FREECAD ASSEMBLY — COMPONENT RECIPES ("composit_stand9")

This assembly document has 29 components, labeled P0..P28 below (a component is one placed body or linked part). 28 of them carry a construction recipe — the FreeCAD feature program that regenerates the part from scratch, quoted from this document or its linked companion documents; the rest are supplied as boundary geometry only. No exploded tour is included for this assembly.
COMPONENT P0 — recipe-attached ("back", modeled in this document).
Construction recipe (the document's own serialized feature program — sketch geometry with constraints, then the solid features built on it; lengths are millimeters unless a unit is written):

FEATURE [PartDesign::SubShapeBinder] Binder001
  BindCopyOnChange = 0
  BindMode = 0
  ClaimChildren = true
  Context = -> Body001 [Binder001.]
  Fuse = false
  MakeFace = true
  OffsetFill = false
  OffsetIntersection = false
  OffsetJoinType = 0
  OffsetOpenResult = false
  PartialLoad = false
  Relative = false
  Support = -> [Connect001]
  _Version = 2
FEATURE [PartDesign::FeaturePython] BaseBend001  # WARN: FeaturePython — macro-defined, semantics opaque (R4)
  BendSide = 1
  BendSketch = -> Binder001
  MidPlane = false
  Reverse = false
  Suppressed = false
  length = 715
  radius = 0.1
  thickness = 0.3
  expr: length = <<BaseBend>>.length
FEATURE [Sketcher::SketchObject] Sketch031
  AttachmentOffset = pos=(0,715,0) rot=(0,0,1;0rad)
  FullyConstrained = true
  MapMode = 5
  Placement = pos=(0,0,715) rot=(0.57735,0.57735,0.57735;2.0944rad)
  expr: .AttachmentOffset.Base.y = <<BaseBend001>>.length
  expr: Constraints[10] = <<back_base_sketch>>.Constraints.side
  sketch-geometry (4):
    g0: LineSegment StartX=3 StartY=0 StartZ=0 EndX=3 EndY=-3 EndZ=0
    g1: LineSegment StartX=3 StartY=-3 StartZ=0 EndX=15 EndY=-3 EndZ=0
    g2: LineSegment StartX=15 StartY=-3 StartZ=0 EndX=15 EndY=0 EndZ=0
    g3: LineSegment StartX=15 StartY=0 StartZ=0 EndX=3 EndY=0 EndZ=0
  constraints (12):
    c: Coincident(g0,g1)
    c: Coincident(g1,g2)
    c: Coincident(g2,g3)
    c: Coincident(g3,g0)
    c: Vertical(g0)
    c: Vertical(g2)
    c: Horizontal(g1)
    c: Horizontal(g3)
    c: PointOnObject(g0,g-1)
    c: DistanceX(g0) = 3
    c: DistanceX(g2) = 15
    c: DistanceY(g0) = -3
FEATURE [PartDesign::CoordinateSystem] Local_CS010  label="back_LCS"
  AttacherType = Attacher::AttachEngine3D
  AttachmentSupport = -> [XY_Plane001]
  MapMode = 5
FEATURE [PartDesign::CoordinateSystem] Local_CS011  label="back_electric_shield_LCS"
  AttacherType = Attacher::AttachEngine3D
  AttachmentOffset = pos=(319.563,80,470) rot=(0.57735,0.57735,0.57735;2.0944rad)
  AttachmentSupport = -> [XY_Plane001]
  MapMode = 5
  Placement = pos=(319.563,80,470) rot=(0.57735,0.57735,0.57735;2.0944rad)
  expr: AttachmentOffset = <<electric_shield_placement>>.Placement
FEATURE [PartDesign::FeaturePython] Extend004  # WARN: FeaturePython — macro-defined, semantics opaque (R4)
  BaseFeature = -> BaseBend001
  Offset = 0.02
  Refine = true
  Suppressed = false
  UseSubtraction = false
  baseObject = -> BaseBend001 [Face1]
  gap1 = 0
  gap2 = 0
  length = 0
FEATURE [PartDesign::FeaturePython] Bend009  # WARN: FeaturePython — macro-defined, semantics opaque (R4)
  AutoMiter = false
  BaseFeature = -> Extend004
  BendType = 0
  LengthList = [20]
  LengthSpec = 0
  ReliefFactor = 0.7
  Suppressed = false
  UseReliefFactor = false
  angle = 90
  baseObject = -> Extend004 [Edge44]
  bendAList = [90]
  extend1 = 0
  extend2 = 0
  gap1 = 3
  gap2 = 3
  invert = true
  kfactor = 0.5
  length = 20
  maxExtendDist = 5
  minGap = 0.2
  minReliefGap = 1
  miterangle1 = 45
  miterangle2 = 45
  offset = 0
  radius = 0.1
  reliefType = 0
  reliefd = 1
  reliefw = 0.8
  sketchflip = false
  sketchinvert = false
  unfold = false
  expr: radius = BaseBend.radius
FEATURE [PartDesign::Pocket] Pocket003
  BaseFeature = -> Bend009
  Direction = (-1,0,0)
  Length = 5
  Length2 = 5
  Midplane = true
  Profile = -> Sketch031
  ReferenceAxis = -> Sketch031 [N_Axis]
  Suppressed = false
  Type = 1
FEATURE [PartDesign::Boolean] Boolean005
  BaseFeature = -> Pocket003
  Group = -> [Compound007]
  Suppressed = false
  Type = 1
  UsePlacement = true
FEATURE [PartDesign::Boolean] Boolean006
  BaseFeature = -> Boolean005
  Group = -> [Compound008]
  Refine = true
  Suppressed = false
  Type = 0
  UsePlacement = true
FEATURE [PartDesign::Body] Body001  label="back"
  Group = -> [Binder001,BaseBend001,Sketch031,Extend004,Bend009,Pocket003,Boolean005,Boolean006,Local_CS010,Local_CS011]
  Origin = -> Origin001
  Tip = -> Boolean006
COMPONENT P1 — recipe-attached ("lamp_holder", modeled in this document).
Construction recipe (the document's own serialized feature program — sketch geometry with constraints, then the solid features built on it; lengths are millimeters unless a unit is written):

FEATURE [PartDesign::SubShapeBinder] Binder006
  BindCopyOnChange = 0
  BindMode = 0
  ClaimChildren = true
  Context = -> Body003 [Binder006.]
  Fuse = false
  MakeFace = true
  OffsetFill = false
  OffsetIntersection = false
  OffsetJoinType = 0
  OffsetOpenResult = false
  PartialLoad = false
  Relative = false
  Support = -> [Sketch007]
  _Version = 2
FEATURE [PartDesign::FeaturePython] BaseBend002  # WARN: FeaturePython — macro-defined, semantics opaque (R4)
  BendSide = 1
  BendSketch = -> Binder006
  MidPlane = false
  Reverse = false
  Suppressed = false
  length = 540
  radius = 2
  thickness = 0.7
FEATURE [PartDesign::CoordinateSystem] Local_CS012  label="lamp_holder_LCS"
  AttacherType = Attacher::AttachEngine3D
  AttachmentSupport = -> [XY_Plane003]
  MapMode = 5
FEATURE [Sketcher::SketchObject] Sketch089
  AttachmentOffset = pos=(0,0,0) rot=(0,1,0;1.5708rad)
  ExternalGeometry = -> [Binder006]
  FullyConstrained = true
  MapMode = 7
  Placement = pos=(299.876,113.48,0) rot=(0.889126,0.323616,0.323616;1.68804rad)
  sketch-geometry (8):
    g0: LineSegment StartX=0 StartY=0 StartZ=0 EndX=32.7 EndY=0 EndZ=0
    g1: LineSegment StartX=0 StartY=33 StartZ=0 EndX=0 EndY=0 EndZ=0
    g2: LineSegment StartX=28.7 StartY=31 StartZ=0 EndX=2 EndY=31 EndZ=0
    g3: ArcOfCircle CenterX=2 CenterY=33 CenterZ=0 NormalX=0 NormalY=0 NormalZ=1 AngleXU=0 Radius=2 StartAngle=3.14159 EndAngle=4.71239
    g4: ArcOfCircle CenterX=28.7 CenterY=29 CenterZ=0 NormalX=0 NormalY=0 NormalZ=1 AngleXU=0 Radius=2 StartAngle=-2.176e-13 EndAngle=1.5708
    g5: GeomPoint X=30.7 Y=31 Z=0
    g6: LineSegment StartX=30.7 StartY=2 StartZ=0 EndX=30.7 EndY=29 EndZ=0
    g7: ArcOfCircle CenterX=32.7 CenterY=2 CenterZ=0 NormalX=0 NormalY=0 NormalZ=1 AngleXU=0 Radius=2 StartAngle=3.14159 EndAngle=4.71239
  constraints (19):
    c: Coincident(g1,g0)
    c: Horizontal(g0)
    c: Vertical(g1)
    c: Coincident(g0,g-1)
    c: Horizontal(g2)
    c: Tangent(g3,g2) = 1.5708
    c: Tangent(g3,g1) = -1.5708
    c: PointOnObject(g5,g2)
    c: Tangent(g2,g4) = -1.5708
    c: DistanceY(g5) = 31
    c: Equal(g4,g3)
    c: Vertical(g6)
    c: Tangent(g7,g0) = -1.5708
    c: Tangent(g7,g6) = 1.5708
    c: Radius(g4) = 2
    c: Tangent(g6,g4) = -1.5708
    c: Equal(g7,g4)
    c: DistanceX(g-3,g6) = 5
    c: PointOnObject(g5,g6)
FEATURE [PartDesign::FeaturePython] SketchOnSheet001  # WARN: FeaturePython — macro-defined, semantics opaque (R4)
  BaseFeature = -> BaseBend002
  Sketch = -> Sketch089
  Suppressed = false
  baseObject = -> BaseBend002 [Face22]
  kfactor = 0.5
FEATURE [PartDesign::Boolean] Boolean003
  BaseFeature = -> SketchOnSheet001
  Group = -> [Compound004]
  Suppressed = false
  Type = 1
  UsePlacement = true
FEATURE [PartDesign::Body] Body003  label="lamp_holder"
  Group = -> [Binder006,BaseBend002,Sketch089,SketchOnSheet001,Boolean003,Local_CS012]
  Origin = -> Origin003
  Tip = -> Boolean003
COMPONENT P2 — recipe-attached ("dropper_fix_PP", modeled in this document).
Construction recipe (the document's own serialized feature program — sketch geometry with constraints, then the solid features built on it; lengths are millimeters unless a unit is written):

FEATURE [PartDesign::SubShapeBinder] Binder007
  BindCopyOnChange = 0
  BindMode = 0
  ClaimChildren = true
  Context = -> Body004 [Binder007.]
  Fuse = false
  MakeFace = true
  OffsetFill = false
  OffsetIntersection = false
  OffsetJoinType = 0
  OffsetOpenResult = false
  PartialLoad = false
  Relative = false
  Support = -> [Connect006]
  _Version = 2
FEATURE [PartDesign::Pad] Pad
  Direction = (0,0,1)
  Length = 5
  Length2 = 10
  Profile = -> Binder007
  Suppressed = false
  Type = 0
FEATURE [PartDesign::CoordinateSystem] Local_CS016  label="dropper_fix_PP_LCS"
  AttacherType = Attacher::AttachEngine3D
  AttachmentSupport = -> [XY_Plane004]
  MapMode = 5
FEATURE [PartDesign::Boolean] Boolean001
  BaseFeature = -> Pad
  Group = -> [Compound002]
  Suppressed = false
  Type = 1
  UsePlacement = true
FEATURE [PartDesign::Body] Body004  label="dropper_fix_PP"
  Group = -> [Binder007,Pad,Boolean001,Local_CS016]
  Origin = -> Origin004
  Tip = -> Boolean001
COMPONENT P3 — recipe-attached ("dropper_fix_composit", modeled in this document).
Construction recipe (the document's own serialized feature program — sketch geometry with constraints, then the solid features built on it; lengths are millimeters unless a unit is written):

FEATURE [PartDesign::SubShapeBinder] Binder008
  BindCopyOnChange = 0
  BindMode = 0
  ClaimChildren = true
  Context = -> Body006 [Binder008.]
  Fuse = false
  MakeFace = true
  OffsetFill = false
  OffsetIntersection = false
  OffsetJoinType = 0
  OffsetOpenResult = false
  PartialLoad = false
  Relative = false
  Support = -> [Connect003]
  _Version = 2
FEATURE [PartDesign::FeaturePython] BaseBend003  # WARN: FeaturePython — macro-defined, semantics opaque (R4)
  BendSide = 0
  BendSketch = -> Binder008
  MidPlane = false
  Reverse = false
  Suppressed = false
  length = 100
  radius = 0.1
  thickness = 0.3
FEATURE [PartDesign::FeaturePython] Extend001  # WARN: FeaturePython — macro-defined, semantics opaque (R4)
  BaseFeature = -> BaseBend003
  Offset = 0.02
  Refine = true
  Suppressed = false
  UseSubtraction = false
  baseObject = -> BaseBend003 [Face1]
  gap1 = 0
  gap2 = 0
  length = 0
FEATURE [PartDesign::FeaturePython] Bend001  # WARN: FeaturePython — macro-defined, semantics opaque (R4)
  AutoMiter = true
  BaseFeature = -> Extend001
  BendType = 0
  LengthList = [20]
  LengthSpec = 0
  ReliefFactor = 0.7
  Suppressed = false
  UseReliefFactor = false
  angle = 90
  baseObject = -> Extend001 [Edge11,Edge9,Edge8,Edge6]
  bendAList = [90]
  extend1 = 0
  extend2 = 0
  gap1 = 0
  gap2 = 0
  invert = true
  kfactor = 0.5
  length = 20
  maxExtendDist = 5
  minGap = 0.2
  minReliefGap = 1
  miterangle1 = 0
  miterangle2 = 0
  offset = 0
  radius = 0.1
  reliefType = 0
  reliefd = 1
  reliefw = 0.8
  sketchflip = false
  sketchinvert = false
  unfold = false
  expr: radius = BaseBend003.radius
FEATURE [Sketcher::SketchObject] Sketch022
  ExternalGeometry = -> [Binder008]
  FullyConstrained = true
  MapMode = 5
  sketch-geometry (5):
    g0: LineSegment StartX=313.563 StartY=108.778 StartZ=0 EndX=313.82 EndY=108.472 EndZ=0
    g1: LineSegment StartX=313.82 StartY=108.472 StartZ=0 EndX=313.563 EndY=108.256 EndZ=0
    g2: LineSegment StartX=313.563 StartY=108.256 StartZ=0 EndX=313.563 EndY=108.778 EndZ=0
    g3: LineSegment StartX=313.563 StartY=108.256 StartZ=0 EndX=313.306 EndY=108.563 EndZ=0
    g4: LineSegment StartX=313.306 StartY=108.563 StartZ=0 EndX=313.563 EndY=108.778 EndZ=0
  constraints (13):
    c: Coincident(g0,g-3)
    c: Coincident(g1,g0)
    c: Coincident(g2,g1)
    c: Coincident(g2,g0)
    c: Vertical(g2)
    c: Distance(g0) = 0.4
    c: Coincident(g1,g3)
    c: PointOnObject(g3,g-3)
    c: Coincident(g3,g4)
    c: Coincident(g4,g0)
    c: Perpendicular(g4,g3)
    c: Perpendicular(g0,g1)
    c: Perpendicular(g0,g4)
FEATURE [Sketcher::SketchObject] Sketch023
  ExternalGeometry = -> [Binder008]
  FullyConstrained = true
  MapMode = 5
  sketch-geometry (7):
    g0: LineSegment StartX=313.563 StartY=108.778 StartZ=0 EndX=313.563 EndY=127 EndZ=0
    g1: LineSegment StartX=313.563 StartY=127 StartZ=0 EndX=310.563 EndY=127 EndZ=0
    g2: LineSegment StartX=310.563 StartY=127 StartZ=0 EndX=310.563 EndY=106.261 EndZ=0
    g3: LineSegment StartX=310.563 StartY=106.261 StartZ=0 EndX=310.82 EndY=105.955 EndZ=0
    g4: LineSegment StartX=310.82 StartY=105.955 StartZ=0 EndX=313.563 EndY=108.256 EndZ=0
    g5: LineSegment StartX=313.563 StartY=108.256 StartZ=0 EndX=313.563 EndY=108.778 EndZ=0
    g6: LineSegment StartX=313.563 StartY=127 StartZ=0 EndX=313.563 EndY=130 EndZ=0
  constraints (19):
    c: Coincident(g-4,g0)
    c: PointOnObject(g0,g-3)
    c: Coincident(g0,g1)
    c: Coincident(g1,g2)
    c: PointOnObject(g2,g-4)
    c: Vertical(g2)
    c: Coincident(g2,g3)
    c: Coincident(g3,g4)
    c: Coincident(g4,g5)
    c: Coincident(g5,g0)
    c: DistanceY(g0,g-3) = 3
    c: Coincident(g6,g0)
    c: Coincident(g6,g-3)
    c: Equal(g6,g1)
    c: Distance(g3) = 0.4
    c: Vertical(g5)
    c: Horizontal(g1)
    c: Perpendicular(g4,g3)
    c: Perpendicular(g-4,g3)
FEATURE [Sketcher::SketchObject] Sketch035
  AttachmentOffset = pos=(0,0,0) rot=(0,1,0;1.5708rad)
  AttachmentSupport = -> [Binder008]
  FullyConstrained = true
  MapMode = 7
  Placement = pos=(106.939,-64.6,0) rot=(0.889126,0.323616,0.323616;1.68804rad)
  sketch-geometry (2):
    g0: Circle CenterX=8 CenterY=16 CenterZ=0 NormalX=0 NormalY=0 NormalZ=1 AngleXU=0 Radius=1.7
    g1: Circle CenterX=262 CenterY=16 CenterZ=0 NormalX=0 NormalY=0 NormalZ=1 AngleXU=0 Radius=1.7
  constraints (6):
    c: Diameter(g0) = 3.4
    c: DistanceX(g0) = 8
    c: DistanceY(g0) = 16
    c: Equal(g0,g1)
    c: Horizontal(g1,g0)
    c: DistanceX(g1) = 262
FEATURE [Sketcher::SketchObject] Sketch036
  ExternalGeometry = -> [Binder008]
  FullyConstrained = true
  MapMode = 5
  sketch-geometry (8):
    g0: LineSegment StartX=107.084 StartY=-65 StartZ=0 EndX=110.66 EndY=-62 EndZ=0
    g1: LineSegment StartX=105.847 StartY=-61.6 StartZ=0 EndX=105.847 EndY=-65 EndZ=0
    g2: LineSegment StartX=105.847 StartY=-65 StartZ=0 EndX=107.084 EndY=-65 EndZ=0
    g3: LineSegment StartX=106.939 StartY=-65 StartZ=0 EndX=106.939 EndY=-64.6 EndZ=0
    g4: LineSegment StartX=106.939 StartY=-64.6 StartZ=0 EndX=107.196 EndY=-64.9064 EndZ=0
    g5: LineSegment StartX=105.847 StartY=-61.6 StartZ=0 EndX=107.084 EndY=-65 EndZ=0
    g6: LineSegment StartX=110.66 StartY=-62 StartZ=0 EndX=110.402 EndY=-61.6936 EndZ=0
    g7: LineSegment StartX=110.402 StartY=-61.6936 StartZ=0 EndX=105.847 EndY=-61.6 EndZ=0
  constraints (23):
    c: Coincident(g7,g1)
    c: Vertical(g1)
    c: Coincident(g1,g2)
    c: Coincident(g2,g0)
    c: Horizontal(g2)
    c: Parallel(g0,g-3)
    c: DistanceY(g1,g1) = 3.4
    c: Distance(g0,g-3) = 0.4
    c: PointOnObject(g3,g2)
    c: Coincident(g3,g-3)
    c: Coincident(g3,g4)
    c: PointOnObject(g4,g0)
    c: Equal(g3,g4)
    c: Vertical(g3)
    c: Perpendicular(g-3,g4)
    c: Coincident(g5,g1)
    c: Coincident(g5,g0)
    c: PointOnObject(g3,g5)
    c: DistanceY(g0,g6) = 3
    c: Coincident(g0,g6)
    c: Coincident(g6,g7)
    c: Perpendicular(g-3,g6)
    c: PointOnObject(g6,g-3)
FEATURE [PartDesign::CoordinateSystem] Local_CS013  label="dropper_fix_composit_LCS"
  AttacherType = Attacher::AttachEngine3D
  AttachmentSupport = -> [XY_Plane006]
  MapMode = 5
FEATURE [PartDesign::CoordinateSystem] Local_CS014  label="dr_fix_c_dr_fix_PP_LCS"
  AttacherType = Attacher::AttachEngine3D
  AttachmentOffset = pos=(0,0,3) rot=(0,0,1;0rad)
  AttachmentSupport = -> [XY_Plane006]
  MapMode = 5
  Placement = pos=(0,0,3) rot=(0,0,1;0rad)
FEATURE [PartDesign::SubtractiveCylinder] Cylinder004
  Angle = 360
  AttacherType = Attacher::AttachEngine3D
  AttachmentOffset = pos=(0,-30,0) rot=(0,0,1;0rad)
  AttachmentSupport = -> [XY_Plane006]
  BaseFeature = -> Bend001
  FirstAngle = 0
  Height = 10
  MapMode = 5
  Placement = pos=(0,-30,0) rot=(0,0,1;0rad)
  Radius = 4
  SecondAngle = 0
  Suppressed = false
FEATURE [PartDesign::Pocket] Pocket
  BaseFeature = -> Cylinder004
  Direction = (0,0,-1)
  Length = 5
  Length2 = 5
  Midplane = true
  Placement = pos=(0,-30,0) rot=(0,0,1;0rad)
  Profile = -> Sketch022
  ReferenceAxis = -> Sketch022 [N_Axis]
  Suppressed = false
  Type = 1
FEATURE [PartDesign::Pocket] Pocket001
  BaseFeature = -> Pocket
  Direction = (0,0,-1)
  Length = 5
  Length2 = 5
  Midplane = true
  Placement = pos=(0,-30,0) rot=(0,0,1;0rad)
  Profile = -> Sketch023
  ReferenceAxis = -> Sketch023 [N_Axis]
  Suppressed = false
  Type = 1
FEATURE [PartDesign::Pocket] Pocket005
  BaseFeature = -> Pocket001
  Direction = (0,0,-1)
  Length = 5
  Length2 = 5
  Midplane = true
  Placement = pos=(0,-30,0) rot=(0,0,1;0rad)
  Profile = -> Sketch036
  ReferenceAxis = -> Sketch036 [N_Axis]
  Suppressed = false
  Type = 1
FEATURE [PartDesign::Mirrored] Mirrored
  BaseFeature = -> Pocket005
  MirrorPlane = -> YZ_Plane006
  Originals = -> [Pocket,Pocket005,Pocket001]
  Placement = pos=(0,-30,0) rot=(0,0,1;0rad)
  Suppressed = false
FEATURE [PartDesign::Boolean] Boolean032
  BaseFeature = -> Mirrored
  Group = -> [Compound028]
  Suppressed = false
  Type = 0
  UsePlacement = true
FEATURE [PartDesign::Pocket] Pocket004
  BaseFeature = -> Boolean032
  ClearanceHeight = 10
  Direction = (-0.642788,0.766044,2e-16)
  Length = 5
  Length2 = 5
  Profile = -> Sketch035
  ReferenceAxis = -> Sketch035 [N_Axis]
  Reversed = true
  SafeHeight = 10
  Suppressed = false
  Type = 1
FEATURE [Sketcher::SketchObject] Sketch106
  AttachmentOffset = pos=(1,0,0) rot=(0,1,0;1.5708rad)
  AttachmentSupport = -> [Binder008]
  FullyConstrained = false
  MapMode = 7
  Placement = pos=(107.581,-65.366,-2e-16) rot=(0.889126,0.323616,0.323616;1.68804rad)
  sketch-geometry (4):
    g0: LineSegment StartX=3.60569 StartY=0.4 StartZ=0 EndX=15.6706 EndY=21.297 EndZ=0
    g1: LineSegment StartX=19.3345 StartY=0.4 StartZ=0 EndX=3.60569 EndY=0.4 EndZ=0
    g2: LineSegment StartX=15.6706 StartY=21.297 StartZ=0 EndX=19.3345 EndY=21.297 EndZ=0
    g3: LineSegment StartX=19.3345 StartY=21.297 StartZ=0 EndX=19.3345 EndY=0.4 EndZ=0
  constraints (10):
    c: Coincident(g0,g2)
    c: Coincident(g3,g1)
    c: Coincident(g0,g1)
    c: DistanceX(g0) = 3.60569
    c: DistanceY(g0) = 0.4
    c: Angle(g0) = 1.0472
    c: DistanceY(g0) = 21.297
    c: Horizontal(g1)
    c: Coincident(g2,g3)
    c: Horizontal(g2)
FEATURE [PartDesign::Pocket] Pocket021
  BaseFeature = -> Pocket004
  Direction = (-0.642788,0.766044,2e-16)
  Length = 5
  Length2 = 5
  Profile = -> Sketch106
  ReferenceAxis = -> Sketch106 [N_Axis]
  Reversed = true
  Suppressed = false
  Type = 0
FEATURE [PartDesign::Mirrored] Mirrored001
  BaseFeature = -> Pocket021
  MirrorPlane = -> YZ_Plane006
  Originals = -> [Pocket004,Pocket021]
  Refine = true
  Suppressed = false
FEATURE [PartDesign::Boolean] Boolean002
  BaseFeature = -> Mirrored001
  ClearanceHeight = 10
  Group = -> [Compound003]
  SafeHeight = 10
  Suppressed = false
  Type = 1
  UsePlacement = true
FEATURE [PartDesign::Body] Body006  label="dropper_fix_composit"
  Group = -> [Binder008,BaseBend003,Extend001,Bend001,Sketch022,Cylinder004,Pocket,Pocket001,Pocket005,Mirrored,Boolean032,Sketch023,Pocket004,Sketch036,Local_CS013,Local_CS014,Sketch106,Pocket021,Mirrored001,Sketch035,Boolean002]
  Origin = -> Origin006
  Tip = -> Boolean002
COMPONENT P4 — recipe-attached ("Body007", modeled in this document).
Construction recipe (the document's own serialized feature program — sketch geometry with constraints, then the solid features built on it; lengths are millimeters unless a unit is written):

FEATURE [PartDesign::SubShapeBinder] Binder009
  BindCopyOnChange = 0
  BindMode = 0
  ClaimChildren = true
  Context = -> Body007 [Binder009.]
  Fuse = false
  MakeFace = true
  OffsetFill = false
  OffsetIntersection = false
  OffsetJoinType = 0
  OffsetOpenResult = false
  PartialLoad = false
  Relative = true
  Support = -> [Cut]
  _Version = 2
FEATURE [PartDesign::FeaturePython] BaseBend004  # WARN: FeaturePython — macro-defined, semantics opaque (R4)
  BendSide = 1
  BendSketch = -> Binder009
  MidPlane = false
  Reverse = true
  Suppressed = false
  length = 100
  radius = 0.1
  thickness = 0.3
FEATURE [PartDesign::FeaturePython] Bend003  # WARN: FeaturePython — macro-defined, semantics opaque (R4)
  AutoMiter = false
  BaseFeature = -> BaseBend004
  BendType = 0
  LengthList = [20]
  LengthSpec = 1
  ReliefFactor = 0.7
  Suppressed = false
  UseReliefFactor = false
  angle = 90
  baseObject = -> BaseBend004 [Edge15,Edge18,Edge21,Edge23]
  bendAList = [90]
  extend1 = 0
  extend2 = 0
  gap1 = 5
  gap2 = 5
  invert = false
  kfactor = 0.5
  length = 20
  maxExtendDist = 0
  minGap = 0.2
  minReliefGap = 0
  miterangle1 = 45
  miterangle2 = 45
  offset = 0
  radius = 0.1
  reliefType = 0
  reliefd = 0
  reliefw = 0
  sketchflip = false
  sketchinvert = false
  unfold = false
  expr: radius = BaseBend004.radius
FEATURE [PartDesign::Boolean] Boolean017
  BaseFeature = -> Bend003
  Group = -> [Compound025]
  Suppressed = false
  Type = 1
  UsePlacement = true
FEATURE [PartDesign::Body] Body007
  Group = -> [Binder009,BaseBend004,Bend003,Boolean017]
  Origin = -> Origin007
  Tip = -> Boolean017
COMPONENT P5 — recipe-attached ("pump_holder", modeled in this document).
Construction recipe (the document's own serialized feature program — sketch geometry with constraints, then the solid features built on it; lengths are millimeters unless a unit is written):

FEATURE [PartDesign::SubShapeBinder] Binder011
  BindCopyOnChange = 0
  BindMode = 0
  ClaimChildren = true
  Context = -> Body008 [Binder011.]
  Fuse = false
  MakeFace = true
  OffsetFill = false
  OffsetIntersection = false
  OffsetJoinType = 0
  OffsetOpenResult = false
  PartialLoad = false
  Placement = pos=(0,0,0) rot=(0.57735,0.57735,0.57735;2.0944rad)
  Relative = false
  Support = -> [Sketch013]
  _Version = 2
  expr: Placement = <<pump_holder_base_sketch>>.Placement
FEATURE [PartDesign::FeaturePython] BaseBend005  label="pump_holder_BaseBend"  # WARN: FeaturePython — macro-defined, semantics opaque (R4)
  BendSide = 1
  BendSketch = -> Binder011
  MidPlane = true
  Reverse = false
  Suppressed = false
  length = 410
  radius = 2
  thickness = 0.7
FEATURE [Sketcher::SketchObject] Sketch015
  AttachmentOffset = pos=(205,0,42) rot=(0,0.707107,0.707107;3.14159rad)
  FullyConstrained = true
  MapMode = 7
  Placement = pos=(205,43.3015,70.6985) rot=(0,0.382683,0.92388;3.14159rad)
  expr: .AttachmentOffset.Base.x = <<pump_holder_BaseBend>>.length / 2
  sketch-geometry (8):
    g0: LineSegment StartX=19 StartY=-25 StartZ=0 EndX=19 EndY=0 EndZ=0
    g1: LineSegment StartX=0 StartY=0 StartZ=0 EndX=0 EndY=-35 EndZ=0
    g2: LineSegment StartX=19 StartY=0 StartZ=0 EndX=0 EndY=0 EndZ=0
    g3: GeomPoint X=19 Y=0 Z=0
    g4: LineSegment StartX=5 StartY=-30 StartZ=0 EndX=14 EndY=-30 EndZ=0
    g5: ArcOfCircle CenterX=5 CenterY=-35 CenterZ=0 NormalX=0 NormalY=0 NormalZ=1 AngleXU=0 Radius=5 StartAngle=1.5708 EndAngle=3.14159
    g6: ArcOfCircle CenterX=14 CenterY=-25 CenterZ=0 NormalX=0 NormalY=0 NormalZ=1 AngleXU=0 Radius=5 StartAngle=4.71239 EndAngle=6.28319
    g7: GeomPoint X=19 Y=-30 Z=0
  constraints (20):
    c: Vertical(g0)
    c: Vertical(g1)
    c: DistanceX(g1,g7) = 19
    c: Horizontal(g2)
    c: PointOnObject(g3,g0)
    c: PointOnObject(g3,g2)
    c: Coincident(g1,g2)
    c: Horizontal(g4)
    c: Tangent(g1,g5) = -1.5708
    c: Tangent(g5,g4) = 1.5708
    c: PointOnObject(g1,g-2)
    c: Coincident(g0,g2)
    c: Tangent(g0,g6) = -1.5708
    c: Tangent(g4,g6) = -1.5708
    c: Equal(g6,g5)
    c: Radius(g6) = 5
    c: PointOnObject(g7,g4)
    c: PointOnObject(g7,g0)
    c: DistanceY(g7,g0) = 30
    c: PointOnObject(g0,g-1)
FEATURE [Sketcher::SketchObject] Sketch039
  AttachmentOffset = pos=(0,0,69.9077) rot=(0,0,1;0rad)
  AttachmentSupport = -> [XY_Plane008]
  ExternalGeometry = -> [Sketch015]
  FullyConstrained = true
  MapMode = 5
  Placement = pos=(0,0,69.9077) rot=(0,0,1;0rad)
  expr: .AttachmentOffset.Base.z = <<Sketch015>>.Placement.Base.z - <<pump_holder_base_sketch>>.Constraints.bend_height
  expr: Constraints[21] = <<pump_holder_base_sketch>>.Constraints.bend_length
  sketch-geometry (12):
    g0: LineSegment StartX=187 StartY=45.3107 StartZ=0 EndX=187 EndY=62.4357 EndZ=0
    g1: LineSegment StartX=190.75 StartY=62.4357 StartZ=0 EndX=190.75 EndY=56.3107 EndZ=0
    g2: LineSegment StartX=205 StartY=45.3107 StartZ=0 EndX=205 EndY=62.4357 EndZ=0
    g3: LineSegment StartX=201.25 StartY=62.4357 StartZ=0 EndX=201.25 EndY=56.3107 EndZ=0
    g4: ArcOfCircle CenterX=196 CenterY=56.3107 CenterZ=0 NormalX=0 NormalY=0 NormalZ=1 AngleXU=0 Radius=5.25 StartAngle=3.14159 EndAngle=6.28319
    g5: ArcOfCircle CenterX=203.125 CenterY=62.4357 CenterZ=0 NormalX=0 NormalY=0 NormalZ=1 AngleXU=0 Radius=1.875 StartAngle=-9e-16 EndAngle=3.14159
    g6: ArcOfCircle CenterX=188.875 CenterY=62.4357 CenterZ=0 NormalX=0 NormalY=0 NormalZ=1 AngleXU=0 Radius=1.875 StartAngle=-1.8e-15 EndAngle=3.14159
    g7: LineSegment StartX=203.125 StartY=64.3107 StartZ=0 EndX=188.875 EndY=64.3107 EndZ=0
    g8: LineSegment StartX=205 StartY=45.3107 StartZ=0 EndX=187 EndY=45.3107 EndZ=0
    g9: LineSegment StartX=186 StartY=43.3015 StartZ=0 EndX=186 EndY=45.3107 EndZ=0
    g10: LineSegment StartX=186 StartY=45.3107 StartZ=0 EndX=187 EndY=45.3107 EndZ=0
    g11: LineSegment StartX=205 StartY=43.3015 StartZ=0 EndX=205 EndY=45.3107 EndZ=0
  constraints (30):
    c: Tangent(g4,g3) = 1.5708
    c: Tangent(g4,g1) = -1.5708
    c: Tangent(g6,g0) = 1.5708
    c: Tangent(g6,g1) = 1.5708
    c: Tangent(g5,g3) = -1.5708
    c: Tangent(g5,g2) = -1.5708
    c: Equal(g6,g5)
    c: Diameter(g4) = 10.5
    c: Tangent(g7,g5) = -1.5708
    c: Coincident(g0,g8)
    c: Distance(g4,g7) = 8
    c: Parallel(g2,g0)
    c: Parallel(g0,g3)
    c: Parallel(g3,g1)
    c: Perpendicular(g2,g7)
    c: Perpendicular(g2,g8)
    c: Tangent(g7,g6) = -1.5708
    c: Coincident(g2,g8)
    c: Coincident(g-3,g9)
    c: Coincident(g9,g10)
    c: Coincident(g10,g0)
    c: DistanceY(g9,g9) = 2.00919
    c: Perpendicular(g10,g9)
    c: Parallel(g10,g8)
    c: Coincident(g11,g-3)
    c: Coincident(g2,g11)
    c: Equal(g11,g9)
    c: Parallel(g11,g9)
    c: Distance(g10) = 1
    c: Distance(g4,g8) = 11
FEATURE [Sketcher::SketchObject] Sketch040
  AttachmentOffset = pos=(0,0,0) rot=(1,0,0;1.5708rad)
  AttachmentSupport = -> [Binder011]
  FullyConstrained = true
  MapMode = 7
  Placement = pos=(0,73,41) rot=(1,0,0;2.35619rad)
  sketch-geometry (4):
    g0: ArcOfCircle CenterX=185 CenterY=8 CenterZ=0 NormalX=0 NormalY=0 NormalZ=1 AngleXU=0 Radius=1.5 StartAngle=3.14159 EndAngle=6.28319
    g1: ArcOfCircle CenterX=185 CenterY=11 CenterZ=0 NormalX=0 NormalY=0 NormalZ=1 AngleXU=0 Radius=1.5 StartAngle=-9e-16 EndAngle=3.14159
    g2: LineSegment StartX=183.5 StartY=8 StartZ=0 EndX=183.5 EndY=11 EndZ=0
    g3: LineSegment StartX=186.5 StartY=8 StartZ=0 EndX=186.5 EndY=11 EndZ=0
  constraints (10):
    c: Tangent(g0,g2) = 1.5708
    c: Tangent(g0,g3) = -1.5708
    c: Tangent(g1,g2) = 1.5708
    c: Tangent(g1,g3) = -1.5708
    c: Equal(g0,g1)
    c: Vertical(g3)
    c: Radius(g1) = 1.5
    c: DistanceY(g3,g3) = 3
    c: DistanceX(g0) = 185
    c: DistanceY(g0) = 8
FEATURE [Sketcher::SketchObject] Sketch041
  ExternalGeometry = -> [Binder011,Sketch039]
  FullyConstrained = true
  MapMode = 5
  Placement = pos=(0,0,0) rot=(0.57735,0.57735,0.57735;2.0944rad)
  sketch-geometry (1):
    g0: LineSegment StartX=15 StartY=99 StartZ=0 EndX=15 EndY=0 EndZ=0
  constraints (5):
    c: Coincident(g0,g-3)
    c: PointOnObject(g0,g-1)
    c: Vertical(g0)
    c: Distance(g-4,g0) = 47.4357
    c: Distance(g-5,g0) = 36.0607
FEATURE [Sketcher::SketchObject] Sketch100
  AttachmentSupport = -> [YZ_Plane008]
  ExternalGeometry = -> [Binder011]
  FullyConstrained = true
  MapMode = 5
  Placement = pos=(0,0,0) rot=(0.57735,0.57735,0.57735;2.0944rad)
  sketch-geometry (1):
    g0: LineSegment StartX=39 StartY=75 StartZ=0 EndX=39 EndY=0 EndZ=0
  constraints (4):
    c: PointOnObject(g0,g-3)
    c: PointOnObject(g0,g-1)
    c: Vertical(g0)
    c: DistanceY(g0,g0) = 75
FEATURE [PartDesign::CoordinateSystem] Local_CS032
  AttacherType = Attacher::AttachEngine3D
  AttachmentOffset = pos=(159,0,0) rot=(-1,0,0;0.785398rad)
  AttachmentSupport = -> [Sketch100]
  MapMode = 7
  Placement = pos=(159,39,75) rot=(-1,0,0;0.785398rad)
FEATURE [Sketcher::SketchObject] Sketch101
  AttachmentSupport = -> [Local_CS032]
  FullyConstrained = true
  MapMode = 5
  Placement = pos=(159,39,75) rot=(-1,0,0;0.785398rad)
  sketch-geometry (2):
    g0: Circle CenterX=22 CenterY=15.6586 CenterZ=0 NormalX=0 NormalY=0 NormalZ=1 AngleXU=0 Radius=1.7
    g1: Circle CenterX=-22 CenterY=15.6586 CenterZ=0 NormalX=0 NormalY=0 NormalZ=1 AngleXU=0 Radius=1.7
  constraints (5):
    c: Symmetric(g0,g1,g-2)
    c: Equal(g0,g1)
    c: DistanceX(g1,g-1) = 22
    c: DistanceY(g1,g-1) = -15.6586
    c: Diameter(g0) = 3.4
FEATURE [Sketcher::SketchObject] Sketch102
  AttachmentSupport = -> [Local_CS032]
  ExternalGeometry = -> [Binder011]
  FullyConstrained = true
  MapMode = 5
  Placement = pos=(159,39,75) rot=(-1,0,0;0.785398rad)
  sketch-geometry (11):
    g0: GeomPoint X=0 Y=23.5416 Z=0
    g1: LineSegment StartX=-12.5 StartY=2 StartZ=0 EndX=12.5 EndY=2 EndZ=0
    g2: LineSegment StartX=14.5 StartY=4 StartZ=0 EndX=14.5 EndY=43.0833 EndZ=0
    g3: LineSegment StartX=12.5 StartY=45.0833 StartZ=0 EndX=-12.5 EndY=45.0833 EndZ=0
    g4: LineSegment StartX=-14.5 StartY=43.0833 StartZ=0 EndX=-14.5 EndY=4 EndZ=0
    g5: ArcOfCircle CenterX=-12.5 CenterY=4 CenterZ=0 NormalX=0 NormalY=0 NormalZ=1 AngleXU=0 Radius=2 StartAngle=3.14159 EndAngle=4.71239
    g6: ArcOfCircle CenterX=12.5 CenterY=4 CenterZ=0 NormalX=0 NormalY=0 NormalZ=1 AngleXU=0 Radius=2 StartAngle=4.71239 EndAngle=6.28319
    g7: ArcOfCircle CenterX=12.5 CenterY=43.0833 CenterZ=0 NormalX=0 NormalY=0 NormalZ=1 AngleXU=0 Radius=2 StartAngle=1.407e-13 EndAngle=1.5708
    g8: ArcOfCircle CenterX=-12.5 CenterY=43.0833 CenterZ=0 NormalX=0 NormalY=0 NormalZ=1 AngleXU=0 Radius=2 StartAngle=1.5708 EndAngle=3.14159
    g9: GeomPoint X=-14.5 Y=2 Z=0
    g10: GeomPoint X=14.5 Y=45.0833 Z=0
  constraints (25):
    c: PointOnObject(g0,g-2)
    c: Tangent(g1,g5) = -1.5708
    c: Tangent(g1,g6) = -1.5708
    c: Tangent(g2,g6) = -1.5708
    c: Tangent(g2,g7) = -1.5708
    c: Tangent(g3,g7) = -1.5708
    c: Tangent(g3,g8) = -1.5708
    c: Tangent(g4,g8) = -1.5708
    c: Tangent(g4,g5) = -1.5708
    c: Horizontal(g1)
    c: Horizontal(g3)
    c: Vertical(g2)
    c: Vertical(g4)
    c: Equal(g5,g6)
    c: Equal(g6,g7)
    c: Equal(g7,g8)
    c: PointOnObject(g9,g1)
    c: PointOnObject(g9,g4)
    c: PointOnObject(g10,g2)
    c: PointOnObject(g10,g3)
    c: Symmetric(g9,g10,g0)
    c: Radius(g7) = 2
    c: DistanceY(g10,g-3) = 3
    c: DistanceY(g-1,g9) = 2
    c: DistanceX(g9,g10) = 29
FEATURE [PartDesign::Pocket] Pocket017
  BaseFeature = -> BaseBend005
  Direction = (0,-0.707107,-0.707107)
  Length = 5
  Length2 = 5
  Midplane = true
  Profile = -> Sketch102
  ReferenceAxis = -> Sketch102 [N_Axis]
  Suppressed = false
  Type = 0
FEATURE [PartDesign::Pocket] Pocket018
  BaseFeature = -> Pocket017
  Direction = (0,-0.707107,-0.707107)
  Length = 5
  Length2 = 5
  Midplane = true
  Profile = -> Sketch101
  ReferenceAxis = -> Sketch101 [N_Axis]
  Suppressed = false
  Type = 0
FEATURE [PartDesign::Boolean] Boolean037
  BaseFeature = -> Pocket018
  Group = -> [Compound034]
  Refine = true
  Suppressed = false
  Type = 0
  UsePlacement = true
FEATURE [PartDesign::Boolean] Boolean004
  BaseFeature = -> Boolean037
  Group = -> [Compound006]
  Suppressed = false
  Type = 1
  UsePlacement = true
FEATURE [PartDesign::CoordinateSystem] Local_CS036
  AttacherType = Attacher::AttachEngine3D
  AttachmentSupport = -> [XY_Plane008]
  MapMode = 5
FEATURE [PartDesign::Body] Body008  label="pump_holder"
  Group = -> [Binder011,BaseBend005,Sketch015,Sketch039,Sketch040,Sketch041,Sketch100,Local_CS032,Sketch101,Sketch102,Pocket017,Pocket018,Boolean037,Boolean004,Local_CS036]
  Origin = -> Origin008
  Tip = -> Boolean004
COMPONENT P6 — recipe-attached ("pump_holder_Body", modeled in this document).
Construction recipe (the document's own serialized feature program — sketch geometry with constraints, then the solid features built on it; lengths are millimeters unless a unit is written):

FEATURE [PartDesign::FeatureBase] BaseFeature
  BaseFeature = -> Unfold003
  Suppressed = false
  expr: BaseFeature = <<pump_holder_Unfold>>._self
  expr: Placement = .BaseFeature.Placement
FEATURE [PartDesign::Body] Body009  label="pump_holder_Body"
  Group = -> [BaseFeature]
  Origin = -> Origin009
  Tip = -> BaseFeature
COMPONENT P7 — recipe-attached ("cap_outer", modeled in this document).
Construction recipe (the document's own serialized feature program — sketch geometry with constraints, then the solid features built on it; lengths are millimeters unless a unit is written):

FEATURE [PartDesign::SubShapeBinder] Binder012
  BindCopyOnChange = 0
  BindMode = 0
  ClaimChildren = true
  Context = -> Body010 [Binder012.]
  Fuse = false
  MakeFace = true
  OffsetFill = false
  OffsetIntersection = false
  OffsetJoinType = 0
  OffsetOpenResult = false
  PartialLoad = false
  Relative = false
  Support = -> [Connect007]
  _Version = 2
FEATURE [PartDesign::FeaturePython] BaseBend007  label="cap_outer_BaseBend"  # WARN: FeaturePython — macro-defined, semantics opaque (R4)
  BendSide = 1
  BendSketch = -> Binder012
  MidPlane = false
  Reverse = false
  Suppressed = false
  length = 50
  radius = 0.1
  thickness = 0.3
FEATURE [PartDesign::FeaturePython] Extend002  # WARN: FeaturePython — macro-defined, semantics opaque (R4)
  BaseFeature = -> BaseBend007
  Offset = 0.02
  Refine = true
  Suppressed = false
  UseSubtraction = false
  baseObject = -> BaseBend007 [Face1]
  gap1 = 0
  gap2 = 0
  length = 0
FEATURE [PartDesign::FeaturePython] Bend005  # WARN: FeaturePython — macro-defined, semantics opaque (R4)
  AutoMiter = true
  BaseFeature = -> Extend002
  BendType = 0
  LengthList = [105.5]
  LengthSpec = 1
  ReliefFactor = 0.7
  Suppressed = false
  UseReliefFactor = false
  angle = 90
  baseObject = -> Extend002 [Edge14,Edge29,Edge76,Edge58,Edge73]
  bendAList = [90]
  extend1 = 0
  extend2 = 0
  gap1 = 0
  gap2 = 0
  invert = true
  kfactor = 0.5
  length = 105.5
  maxExtendDist = 5
  minGap = 0.025
  minReliefGap = 0.2
  miterangle1 = 0
  miterangle2 = 0
  offset = 0
  radius = 0.1
  reliefType = 0
  reliefd = 1
  reliefw = 0.8
  sketchflip = false
  sketchinvert = false
  unfold = false
  expr: length = <<cap_base_sketch>>.Constraints.depth / 2
  expr: radius = BaseBend007.radius
FEATURE [PartDesign::Boolean] Boolean008
  BaseFeature = -> Bend005
  Group = -> [BaseBend006]
  Refine = true
  Suppressed = false
  Type = 0
  UsePlacement = true
FEATURE [PartDesign::Boolean] Boolean009
  BaseFeature = -> Boolean008
  Group = -> [Compound011]
  Suppressed = false
  Type = 1
  UsePlacement = true
FEATURE [PartDesign::CoordinateSystem] Local_CS015  label="cap_outer_LCS"
  AttacherType = Attacher::AttachEngine3D
  AttachmentSupport = -> [XY_Plane010]
  MapMode = 5
FEATURE [PartDesign::Body] Body010  label="cap_outer"
  Group = -> [Binder012,BaseBend007,Extend002,Bend005,Boolean008,Boolean009,Local_CS015]
  Origin = -> Origin010
  Tip = -> Boolean009
COMPONENT P8 — recipe-attached ("cap_inner", modeled in this document).
Construction recipe (the document's own serialized feature program — sketch geometry with constraints, then the solid features built on it; lengths are millimeters unless a unit is written):

FEATURE [PartDesign::SubShapeBinder] Binder013
  BindCopyOnChange = 0
  BindMode = 0
  ClaimChildren = true
  Context = -> Body011 [Binder013.]
  Fuse = false
  MakeFace = true
  OffsetFill = false
  OffsetIntersection = false
  OffsetJoinType = 0
  OffsetOpenResult = false
  PartialLoad = false
  Placement = pos=(0,0,47.1) rot=(0,0,1;0rad)
  Relative = true
  Support = -> [Sketch028]
  _Version = 2
  expr: .Placement.Base.z = <<cap_outer_BaseBend>>.length + <<cap_outer_BaseBend>>.radius - 3 mm
FEATURE [PartDesign::FeaturePython] BaseBend008  # WARN: FeaturePython — macro-defined, semantics opaque (R4)
  BendSide = 0
  BendSketch = -> Binder013
  MidPlane = false
  Reverse = false
  Suppressed = false
  length = 100
  radius = 0.1
  thickness = 0.3
FEATURE [PartDesign::FeaturePython] Bend006  # WARN: FeaturePython — macro-defined, semantics opaque (R4)
  AutoMiter = false
  BaseFeature = -> BaseBend008
  BendType = 1
  LengthList = [47]
  LengthSpec = 0
  ReliefFactor = 0.7
  Suppressed = false
  UseReliefFactor = false
  angle = 90
  baseObject = -> BaseBend008 [Edge7,Edge10]
  bendAList = [90]
  extend1 = 0
  extend2 = 0
  gap1 = 0.4
  gap2 = 3
  invert = true
  kfactor = 0.5
  length = 47
  maxExtendDist = 5
  minGap = 0.2
  minReliefGap = 1
  miterangle1 = 0
  miterangle2 = 0
  offset = 0
  radius = 0.1
  reliefType = 0
  reliefd = 1
  reliefw = 0.8
  sketchflip = false
  sketchinvert = false
  unfold = false
  expr: length = <<cap_outer_BaseBend>>.length - 3 mm
  expr: radius = <<cap_outer_BaseBend>>.radius
FEATURE [PartDesign::SubShapeBinder] Binder014
  BindCopyOnChange = 0
  BindMode = 0
  ClaimChildren = true
  Context = -> Body011 [Binder014.]
  Fuse = false
  MakeFace = true
  OffsetFill = false
  OffsetIntersection = false
  OffsetJoinType = 0
  OffsetOpenResult = false
  PartialLoad = false
  Relative = true
  Support = -> [Sketch009]
  _Version = 2
FEATURE [Sketcher::SketchObject] Sketch029
  AttachmentOffset = pos=(0,0,316.563) rot=(0,0,1;0rad)
  ExternalGeometry = -> [Binder014]
  FullyConstrained = true
  MapMode = 5
  Placement = pos=(316.563,0,0) rot=(0.57735,0.57735,0.57735;2.0944rad)
  expr: .AttachmentOffset.Base.z = <<cap_base_sketch>>.Constraints.total_width / 2 - 3 mm
  sketch-geometry (10):
    g0: LineSegment StartX=30 StartY=0 StartZ=0 EndX=45 EndY=0 EndZ=0
    g1: LineSegment StartX=45 StartY=0 StartZ=0 EndX=45 EndY=-3 EndZ=0
    g2: LineSegment StartX=45 StartY=-3 StartZ=0 EndX=42 EndY=-6 EndZ=0
    g3: LineSegment StartX=42 StartY=-6 StartZ=0 EndX=33 EndY=-6 EndZ=0
    g4: LineSegment StartX=33 StartY=-6 StartZ=0 EndX=30 EndY=-3 EndZ=0
    g5: LineSegment StartX=30 StartY=-3 StartZ=0 EndX=30 EndY=0 EndZ=0
    g6: LineSegment StartX=30 StartY=-3 StartZ=0 EndX=37.5 EndY=-3 EndZ=0
    g7: LineSegment StartX=37.5 StartY=-3 StartZ=0 EndX=45 EndY=-3 EndZ=0
    g8: LineSegment StartX=37.5 StartY=-3 StartZ=0 EndX=42 EndY=-6 EndZ=0
    g9: LineSegment StartX=33 StartY=-6 StartZ=0 EndX=37.5 EndY=-3 EndZ=0
  constraints (25):
    c: Coincident(g0,g-3)
    c: Coincident(g0,g-4)
    c: Coincident(g0,g1)
    c: Vertical(g1)
    c: Coincident(g1,g2)
    c: Coincident(g2,g3)
    c: Horizontal(g3)
    c: Coincident(g3,g4)
    c: Coincident(g4,g5)
    c: Coincident(g5,g0)
    c: Vertical(g5)
    c: Equal(g5,g1)
    c: Coincident(g4,g6)
    c: Horizontal(g6)
    c: Coincident(g6,g7)
    c: Coincident(g7,g1)
    c: Coincident(g6,g8)
    c: Coincident(g8,g2)
    c: Coincident(g3,g9)
    c: Coincident(g9,g6)
    c: Equal(g7,g6)
    c: Equal(g9,g8)
    c: DistanceY(g1,g1) = 3
    c: DistanceY(g2,g1) = 3
    c: Angle(g2) = -2.35619
FEATURE [PartDesign::Pad] Pad001
  BaseFeature = -> Bend006
  Direction = (1,0,0)
  Length = 0.3
  Length2 = 10
  Profile = -> Sketch029
  ReferenceAxis = -> Sketch029 [N_Axis]
  Refine = true
  Reversed = true
  Suppressed = false
  Type = 0
FEATURE [Sketcher::SketchObject] Sketch030
  AttachmentOffset = pos=(0,0,316.563) rot=(0,0,1;0rad)
  ExternalGeometry = -> [Sketch029,Binder013]
  FullyConstrained = true
  MapMode = 5
  Placement = pos=(316.563,0,0) rot=(0.57735,0.57735,0.57735;2.0944rad)
  expr: AttachmentOffset = <<Sketch029>>.AttachmentOffset
  sketch-geometry (3):
    g0: LineSegment StartX=153 StartY=46.7 StartZ=0 EndX=45 EndY=0 EndZ=0
    g1: LineSegment StartX=45 StartY=0 StartZ=0 EndX=153 EndY=0 EndZ=0
    g2: LineSegment StartX=153 StartY=0 StartZ=0 EndX=153 EndY=46.7 EndZ=0
  constraints (8):
    c: Coincident(g0,g-3)
    c: Coincident(g0,g1)
    c: PointOnObject(g1,g-1)
    c: Coincident(g1,g2)
    c: Vertical(g2)
    c: Coincident(g2,g0)
    c: DistanceX(g0,g-4) = 0
    c: DistanceY(g0,g-4) = 0.4
FEATURE [PartDesign::Pocket] Pocket002
  BaseFeature = -> Pad001
  Direction = (-1,0,0)
  Length = 5
  Length2 = 5
  Profile = -> Sketch030
  ReferenceAxis = -> Sketch030 [N_Axis]
  Suppressed = false
  Type = 0
FEATURE [PartDesign::Boolean] Boolean010
  BaseFeature = -> Pocket002
  Group = -> [Compound013]
  Suppressed = false
  Type = 1
  UsePlacement = true
FEATURE [PartDesign::CoordinateSystem] Local_CS025
  AttacherType = Attacher::AttachEngine3D
  AttachmentSupport = -> [XY_Plane011]
  MapMode = 5
FEATURE [PartDesign::Body] Body011  label="cap_inner"
  Group = -> [Binder013,BaseBend008,Bend006,Binder014,Sketch029,Pad001,Sketch030,Pocket002,Local_CS025,Boolean010]
  Origin = -> Origin011
  Tip = -> Boolean010
COMPONENT P9 — recipe-attached ("sink", modeled in this document).
Construction recipe (the document's own serialized feature program — sketch geometry with constraints, then the solid features built on it; lengths are millimeters unless a unit is written):

FEATURE [PartDesign::SubShapeBinder] Binder015
  BindCopyOnChange = 0
  BindMode = 0
  ClaimChildren = true
  Context = -> Body012 [Binder015.]
  Fuse = false
  MakeFace = true
  OffsetFill = false
  OffsetIntersection = false
  OffsetJoinType = 0
  OffsetOpenResult = false
  PartialLoad = false
  Relative = false
  Support = -> [Sketch001]
  _Version = 2
FEATURE [PartDesign::CoordinateSystem] Local_CS
  AttacherType = Attacher::AttachEngine3D
  AttachmentOffset = pos=(0,0,0) rot=(0,1,0;1.5708rad)
  MapMode = 7
  Placement = pos=(164.635,0,0) rot=(0.889126,0.323616,0.323616;1.68804rad)
FEATURE [PartDesign::CoordinateSystem] Local_CS001
  AttacherType = Attacher::AttachEngine3D
  AttachmentOffset = pos=(0,0,0) rot=(1,0,0;0.152649rad)
  MapMode = 5
  Placement = pos=(0,0,0) rot=(1,0,0;0.152649rad)
  expr: .AttachmentOffset.Rotation.Angle = <<sink_front_bend_sketch>>.Constraints.angle
FEATURE [PartDesign::CoordinateSystem] Local_CS003
  AttacherType = Attacher::AttachEngine3D
  AttachmentOffset = pos=(0,0,0) rot=(0,1,0;1.5708rad)
  MapMode = 7
  Placement = pos=(-164.635,0,0) rot=(0.889126,-0.323616,-0.323616;1.68804rad)
FEATURE [PartDesign::CoordinateSystem] Local_CS004  label="sink_place"
  AttacherType = Attacher::AttachEngine3D
  MapMode = 5
FEATURE [Sketcher::SketchObject] Sketch005  label="sink_side_line"
  ExternalGeometry = -> [Binder015]
  FullyConstrained = true
  MapMode = 5
  Placement = pos=(164.635,0,0) rot=(0.889126,0.323616,0.323616;1.68804rad)
  sketch-geometry (1):
    g0: LineSegment StartX=-2.84e-14 StartY=0 StartZ=0 EndX=202.244 EndY=20 EndZ=0
  constraints (4):
    c: Coincident(g0,g-3)
    c: Vertical(g0,g-3)
    c: DistanceY(g0) = 20  'height'
    c: Angle(g0) = 0.0985699  'angle'
FEATURE [Sketcher::SketchObject] Sketch006  label="sink_front_bend_sketch"
  ExternalGeometry = -> [Sketch005]
  FullyConstrained = true
  MapMode = 5
  Placement = pos=(0,0,0) rot=(0.57735,0.57735,0.57735;2.0944rad)
  sketch-geometry (3):
    g0: LineSegment StartX=0 StartY=2.91403 StartZ=0 EndX=-4e-15 EndY=0 EndZ=0
    g1: LineSegment StartX=-4e-15 StartY=0 StartZ=0 EndX=2.88014 EndY=0.443099 EndZ=0
    g2: ArcOfCircle CenterX=2.5 CenterY=2.91403 CenterZ=0 NormalX=0 NormalY=0 NormalZ=1 AngleXU=0 Radius=2.5 StartAngle=3.14159 EndAngle=4.86504
  constraints (8):
    c: PointOnObject(g0,g-2)
    c: Coincident(g0,g-3)
    c: Coincident(g0,g1)
    c: Tangent(g2,g1) = -1.5708
    c: Tangent(g2,g0) = -1.5708
    c: Radius(g2) = 2.5
    c: Angle(g1) = 0.152649  'angle'
    c: PointOnObject(g1,g-3)
FEATURE [Sketcher::SketchObject] Sketch044
  ExternalGeometry = -> [Binder015]
  FullyConstrained = true
  MapMode = 7
  Placement = pos=(164.635,0,-2e-15) rot=(0.846388,-0.394677,-0.357572;1.83324rad)
  sketch-geometry (3):
    g0: ArcOfCircle CenterX=-2.5 CenterY=2.81034 CenterZ=0 NormalX=0 NormalY=0 NormalZ=1 AngleXU=0 Radius=2.5 StartAngle=4.59564 EndAngle=6.28319
    g1: LineSegment StartX=-2.79121 StartY=0.327355 StartZ=0 EndX=0 EndY=0 EndZ=0
    g2: LineSegment StartX=0 StartY=0 StartZ=0 EndX=0 EndY=2.81034 EndZ=0
  constraints (7):
    c: PointOnObject(g0,g-2)
    c: Coincident(g1,g-1)
    c: Coincident(g2,g1)
    c: Tangent(g2,g0) = -1.5708
    c: Tangent(g1,g0) = -1.5708
    c: PointOnObject(g0,g-3)
    c: Radius(g0) = 2.5
FEATURE [Sketcher::SketchObject] Sketch045  label="sink_plane_sketch"
  ExternalGeometry = -> [Sketch006,Sketch005,Sketch044]
  FullyConstrained = true
  MapMode = 5
  Placement = pos=(0,0,0) rot=(1,0,0;0.152649rad)
  sketch-geometry (4):
    g0: LineSegment StartX=-163.725 StartY=2.91403 StartZ=0 EndX=163.725 EndY=2.91403 EndZ=0
    g1: LineSegment StartX=163.725 StartY=2.91403 StartZ=0 EndX=317.576 EndY=133.529 EndZ=0
    g2: LineSegment StartX=317.576 StartY=133.529 StartZ=0 EndX=-317.576 EndY=133.529 EndZ=0
    g3: LineSegment StartX=-317.576 StartY=133.529 StartZ=0 EndX=-163.725 EndY=2.91403 EndZ=0
  constraints (14):
    c: Coincident(g0,g1)
    c: Coincident(g1,g2)
    c: Coincident(g2,g3)
    c: Coincident(g3,g0)
    c: Symmetric(g0,g0,g-2)
    c: Symmetric(g2,g1,g-2)
    c: Parallel(g1,g-4)
    c: PointOnObject(g-5,g1)
    c: PointOnObject(g-3,g0)
    c: Distance(g1) = 201.818  'rigth_side'
    c: Distance(g0) = 327.45  'front'
    c: Distance(g2) = 635.153  'end'
    c: Distance(g3) = 201.818  'left_side'
    c: DistanceY(g-4,g1) = 2
FEATURE [PartDesign::Pad] Pad003
  Direction = (0,-0.152057,0.988372)
  Length = 0.5
  Length2 = 10
  Placement = pos=(0,0,0) rot=(1,0,0;0.152649rad)
  Profile = -> Sketch045
  ReferenceAxis = -> Sketch045 [N_Axis]
  Suppressed = false
  Type = 0
FEATURE [Sketcher::SketchObject] Sketch046
  ExternalGeometry = -> [Sketch006]
  FullyConstrained = true
  MapMode = 2
  Placement = pos=(0,0,0) rot=(0.57735,0.57735,0.57735;2.0944rad)
  sketch-geometry (4):
    g0: ArcOfCircle CenterX=2.5 CenterY=2.91403 CenterZ=0 NormalX=0 NormalY=0 NormalZ=1 AngleXU=0 Radius=2.5 StartAngle=3.14159 EndAngle=4.86504
    g1: LineSegment StartX=2.88014 StartY=0.443099 StartZ=0 EndX=2.80411 EndY=0.937285 EndZ=0
    g2: LineSegment StartX=0 StartY=2.91403 StartZ=0 EndX=0.5 EndY=2.91403 EndZ=0
    g3: ArcOfCircle CenterX=2.5 CenterY=2.91403 CenterZ=0 NormalX=0 NormalY=0 NormalZ=1 AngleXU=0 Radius=2 StartAngle=3.14159 EndAngle=4.86504
  constraints (10):
    c: Coincident(g0,g-3)
    c: Tangent(g0,g-3) = -1.5708
    c: Coincident(g0,g1)
    c: Coincident(g0,g2)
    c: Coincident(g3,g0)
    c: Coincident(g3,g2)
    c: Coincident(g3,g1)
    c: Perpendicular(g3,g1)
    c: Distance(g1) = 0.5
    c: Perpendicular(g3,g2)
FEATURE [Sketcher::SketchObject] Sketch047
  ExternalGeometry = -> [Sketch044]
  FullyConstrained = true
  MapMode = 7
  Placement = pos=(163.725,2.88014,0.443099) rot=(0.846388,-0.394677,-0.357572;1.83324rad)
  sketch-geometry (4):
    g0: ArcOfCircle CenterX=0.291206 CenterY=2.48298 CenterZ=0 NormalX=0 NormalY=0 NormalZ=1 AngleXU=0 Radius=2.5 StartAngle=4.59564 EndAngle=6.28319
    g1: LineSegment StartX=3.47e-14 StartY=1.55e-14 StartZ=0 EndX=0.0582413 EndY=0.496596 EndZ=0
    g2: LineSegment StartX=2.79121 StartY=2.48298 StartZ=0 EndX=2.29121 EndY=2.48298 EndZ=0
    g3: ArcOfCircle CenterX=0.291206 CenterY=2.48298 CenterZ=0 NormalX=0 NormalY=0 NormalZ=1 AngleXU=0 Radius=2 StartAngle=4.59564 EndAngle=6.28319
  constraints (10):
    c: Coincident(g0,g-3)
    c: Tangent(g0,g-3) = -1.5708
    c: Coincident(g1,g0)
    c: Coincident(g2,g0)
    c: Coincident(g3,g0)
    c: Coincident(g3,g1)
    c: Coincident(g3,g2)
    c: Distance(g1) = 0.5
    c: Perpendicular(g3,g1)
    c: Perpendicular(g3,g2)
FEATURE [PartDesign::Pad] Pad004
  BaseFeature = -> Pad003
  Direction = (-0.762326,-0.639667,-0.0984104)
  Length = 201.818
  Length2 = 10
  Placement = pos=(0,0,0) rot=(1,0,0;0.152649rad)
  Profile = -> Sketch047
  ReferenceAxis = -> Sketch047 [N_Axis]
  Reversed = true
  Suppressed = false
  Type = 0
  expr: Length = <<sink_plane_sketch>>.Constraints.rigth_side
FEATURE [Sketcher::SketchObject] Sketch048
  ExternalGeometry = -> [Sketch045]
  FullyConstrained = true
  MapMode = 7
  Placement = pos=(-163.725,2.88014,0.443099) rot=(-0.298783,0.640743,0.707232;3.7787rad)
  sketch-geometry (4):
    g0: ArcOfCircle CenterX=0.291206 CenterY=2.48298 CenterZ=0 NormalX=0 NormalY=0 NormalZ=1 AngleXU=0 Radius=2 StartAngle=4.59564 EndAngle=6.28319
    g1: ArcOfCircle CenterX=0.291206 CenterY=2.48298 CenterZ=0 NormalX=0 NormalY=0 NormalZ=1 AngleXU=0 Radius=2.5 StartAngle=4.59564 EndAngle=6.28319
    g2: LineSegment StartX=-4e-16 StartY=0 StartZ=0 EndX=0.0582413 EndY=0.496596 EndZ=0
    g3: LineSegment StartX=2.29121 StartY=2.48298 StartZ=0 EndX=2.79121 EndY=2.48298 EndZ=0
  constraints (12):
    c: Coincident(g1,g0)
    c: Coincident(g1,g-1)
    c: Coincident(g2,g1)
    c: Coincident(g2,g0)
    c: Coincident(g3,g0)
    c: Coincident(g3,g1)
    c: Perpendicular(g0,g3)
    c: Perpendicular(g0,g2)
    c: Perpendicular(g2,g-3)
    c: Horizontal(g3)
    c: Radius(g0) = 2
    c: Distance(g2) = 0.5
FEATURE [PartDesign::Pad] Pad005
  BaseFeature = -> Pad004
  Direction = (-0.762326,0.639667,0.0984104)
  Length = 201.818
  Length2 = 10
  Placement = pos=(0,0,0) rot=(1,0,0;0.152649rad)
  Profile = -> Sketch048
  ReferenceAxis = -> Sketch048 [N_Axis]
  Suppressed = false
  Type = 0
  expr: Length = <<sink_plane_sketch>>.Constraints.left_side
FEATURE [PartDesign::Pad] Pad006
  BaseFeature = -> Pad005
  Direction = (1,0,0)
  Length = 327.45
  Length2 = 10
  Midplane = true
  Placement = pos=(0,0,0) rot=(1,0,0;0.152649rad)
  Profile = -> Sketch046
  ReferenceAxis = -> Sketch046 [N_Axis]
  Suppressed = false
  Type = 0
  expr: Length = <<sink_plane_sketch>>.Constraints.front
FEATURE [Sketcher::SketchObject] Sketch050
  ExternalGeometry = -> [Sketch045,Sketch046]
  FullyConstrained = true
  MapMode = 5
  Placement = pos=(0,0,0) rot=(1,0,0;1.5708rad)
  sketch-geometry (6):
    g0: LineSegment StartX=-163.725 StartY=2.91403 StartZ=0 EndX=-163.725 EndY=80 EndZ=0
    g1: LineSegment StartX=-163.725 StartY=80 StartZ=0 EndX=163.725 EndY=80 EndZ=0
    g2: LineSegment StartX=163.725 StartY=80 StartZ=0 EndX=163.725 EndY=2.91403 EndZ=0
    g3: LineSegment StartX=163.725 StartY=2.91403 StartZ=0 EndX=-163.725 EndY=2.91403 EndZ=0
    g4: LineSegment StartX=-163.725 StartY=0.443099 StartZ=0 EndX=-163.725 EndY=2.91403 EndZ=0
    g5: LineSegment StartX=163.725 StartY=0.443099 StartZ=0 EndX=163.725 EndY=2.91403 EndZ=0
  constraints (16):
    c: Vertical(g0)
    c: Coincident(g0,g1)
    c: Horizontal(g1)
    c: Coincident(g1,g2)
    c: Vertical(g2)
    c: Coincident(g2,g3)
    c: Coincident(g3,g0)
    c: Horizontal(g3)
    c: PointOnObject(g-4,g3)
    c: Coincident(g4,g-3)
    c: Coincident(g4,g0)
    c: Perpendicular(g3,g4)
    c: Coincident(g5,g-3)
    c: Coincident(g5,g2)
    c: Perpendicular(g3,g5)
    c: DistanceY(g1) = 80
FEATURE [PartDesign::Pad] Pad007
  BaseFeature = -> Pad006
  Direction = (0,-1,2e-16)
  Length = 0.5
  Length2 = 10
  Placement = pos=(0,0,0) rot=(1,0,0;0.152649rad)
  Profile = -> Sketch050
  ReferenceAxis = -> Sketch050 [N_Axis]
  Reversed = true
  Suppressed = false
  Type = 0
FEATURE [Sketcher::SketchObject] Sketch049
  ExternalGeometry = -> [Sketch045,Sketch047,Sketch050]
  FullyConstrained = true
  MapMode = 5
  Placement = pos=(164.635,0,0) rot=(0.889126,0.323616,0.323616;1.68804rad)
  sketch-geometry (4):
    g0: LineSegment StartX=0.909926 StartY=2.91403 StartZ=0 EndX=201.749 EndY=22.775 EndZ=0
    g1: LineSegment StartX=0.909926 StartY=2.91403 StartZ=0 EndX=0.909926 EndY=80 EndZ=0
    g2: LineSegment StartX=0.909926 StartY=80 StartZ=0 EndX=201.749 EndY=80 EndZ=0
    g3: LineSegment StartX=201.749 StartY=80 StartZ=0 EndX=201.749 EndY=22.775 EndZ=0
  constraints (11):
    c: Coincident(g0,g-4)
    c: Parallel(g-3,g0)
    c: Equal(g0,g-3)
    c: Coincident(g0,g1)
    c: Vertical(g1)
    c: Coincident(g1,g2)
    c: Horizontal(g2)
    c: Coincident(g2,g3)
    c: Coincident(g3,g0)
    c: Vertical(g3)
    c: Horizontal(g-5,g1)
FEATURE [PartDesign::Pad] Pad008
  BaseFeature = -> Pad007
  Direction = (0.642788,-0.766044,0)
  Length = 0.5
  Length2 = 10
  Placement = pos=(0,0,0) rot=(1,0,0;0.152649rad)
  Profile = -> Sketch049
  ReferenceAxis = -> Sketch049 [N_Axis]
  Reversed = true
  Suppressed = false
  Type = 0
FEATURE [Sketcher::SketchObject] Sketch051
  ExternalGeometry = -> [Binder015]
  FullyConstrained = true
  MapMode = 5
  sketch-geometry (1):
    g0: LineSegment StartX=-319.563 StartY=130 StartZ=0 EndX=-164.635 EndY=0 EndZ=0
  constraints (2):
    c: Symmetric(g0,g-3,g-2)
    c: Symmetric(g0,g-3,g-2)
FEATURE [Sketcher::SketchObject] Sketch052
  ExternalGeometry = -> [Sketch045,Sketch048,Sketch050]
  FullyConstrained = true
  MapMode = 5
  Placement = pos=(-164.635,-1.4e-14,0) rot=(0.889126,-0.323616,-0.323616;1.68804rad)
  sketch-geometry (5):
    g0: LineSegment StartX=-201.749 StartY=22.775 StartZ=0 EndX=-0.909926 EndY=2.91403 EndZ=0
    g1: LineSegment StartX=-0.909926 StartY=2.91403 StartZ=0 EndX=-0.909926 EndY=80 EndZ=0
    g2: LineSegment StartX=-0.909926 StartY=80 StartZ=0 EndX=-201.749 EndY=80 EndZ=0
    g3: LineSegment StartX=-201.749 StartY=80 StartZ=0 EndX=-201.749 EndY=22.775 EndZ=0
    g4: LineSegment StartX=-201.993 StartY=20.3041 StartZ=0 EndX=-201.749 EndY=22.775 EndZ=0
  constraints (13):
    c: Coincident(g0,g-4)
    c: Coincident(g1,g0)
    c: Vertical(g1)
    c: Coincident(g1,g2)
    c: Horizontal(g2)
    c: Coincident(g2,g3)
    c: Coincident(g3,g0)
    c: Vertical(g3)
    c: Coincident(g4,g-3)
    c: Coincident(g4,g0)
    c: Perpendicular(g-3,g4)
    c: Parallel(g-3,g0)
    c: Horizontal(g1,g-5)
FEATURE [PartDesign::Pad] Pad009
  BaseFeature = -> Pad008
  Direction = (-0.642788,-0.766044,0)
  Length = 0.5
  Length2 = 10
  Placement = pos=(0,0,0) rot=(1,0,0;0.152649rad)
  Profile = -> Sketch052
  ReferenceAxis = -> Sketch052 [N_Axis]
  Reversed = true
  Suppressed = false
  Type = 0
FEATURE [Sketcher::SketchObject] Sketch053
  ExternalGeometry = -> [Pad009]
  FullyConstrained = true
  MapMode = 5
  Placement = pos=(0,0,0) rot=(1,0,0;0.152649rad)
  sketch-geometry (28):
    g0: LineSegment StartX=0 StartY=2 StartZ=0 EndX=40.9313 EndY=2 EndZ=0
    g1: LineSegment StartX=40.9313 StartY=2 StartZ=0 EndX=81.8625 EndY=2 EndZ=0
    g2: LineSegment StartX=81.8625 StartY=2 StartZ=0 EndX=122.794 EndY=2 EndZ=0
    g3: LineSegment StartX=122.794 StartY=2 StartZ=0 EndX=163.725 EndY=2 EndZ=0
    g4: ArcOfCircle CenterX=-17 CenterY=2 CenterZ=0 NormalX=0 NormalY=0 NormalZ=1 AngleXU=0 Radius=3 StartAngle=1.5708 EndAngle=4.71239
    g5: ArcOfCircle CenterX=17 CenterY=2 CenterZ=0 NormalX=0 NormalY=0 NormalZ=1 AngleXU=0 Radius=3 StartAngle=4.71239 EndAngle=7.85398
    g6: LineSegment StartX=-17 StartY=5 StartZ=0 EndX=17 EndY=5 EndZ=0
    g7: LineSegment StartX=-17 StartY=-1 StartZ=0 EndX=17 EndY=-1 EndZ=0
    g8: GeomPoint X=-20 Y=2 Z=0
    g9: GeomPoint X=20 Y=2 Z=0
    g10: ArcOfCircle CenterX=106 CenterY=2 CenterZ=0 NormalX=0 NormalY=0 NormalZ=1 AngleXU=0 Radius=3 StartAngle=1.5708 EndAngle=4.71239
    g11: ArcOfCircle CenterX=140 CenterY=2 CenterZ=0 NormalX=0 NormalY=0 NormalZ=1 AngleXU=0 Radius=3 StartAngle=4.71239 EndAngle=7.85398
    g12: LineSegment StartX=106 StartY=5 StartZ=0 EndX=140 EndY=5 EndZ=0
    g13: LineSegment StartX=106 StartY=-1 StartZ=0 EndX=140 EndY=-1 EndZ=0
    g14: ArcOfCircle CenterX=-140 CenterY=2 CenterZ=0 NormalX=0 NormalY=0 NormalZ=1 AngleXU=0 Radius=3 StartAngle=1.5708 EndAngle=4.71239
    g15: ArcOfCircle CenterX=-106 CenterY=2 CenterZ=0 NormalX=0 NormalY=0 NormalZ=1 AngleXU=0 Radius=3 StartAngle=4.71239 EndAngle=7.85398
    g16: LineSegment StartX=-140 StartY=5 StartZ=0 EndX=-106 EndY=5 EndZ=0
    g17: LineSegment StartX=-140 StartY=-1 StartZ=0 EndX=-106 EndY=-1 EndZ=0
    g18: ArcOfCircle CenterX=-78.5 CenterY=2 CenterZ=0 NormalX=0 NormalY=0 NormalZ=1 AngleXU=0 Radius=3 StartAngle=1.5708 EndAngle=4.71239
    g19: ArcOfCircle CenterX=-44.5 CenterY=2 CenterZ=0 NormalX=0 NormalY=0 NormalZ=1 AngleXU=0 Radius=3 StartAngle=4.71239 EndAngle=7.85398
    g20: LineSegment StartX=-78.5 StartY=5 StartZ=0 EndX=-44.5 EndY=5 EndZ=0
    g21: LineSegment StartX=-78.5 StartY=-1 StartZ=0 EndX=-44.5 EndY=-1 EndZ=0
    g22: ArcOfCircle CenterX=44.5 CenterY=2 CenterZ=0 NormalX=0 NormalY=0 NormalZ=1 AngleXU=0 Radius=3 StartAngle=1.5708 EndAngle=4.71239
    g23: ArcOfCircle CenterX=78.5 CenterY=2 CenterZ=0 NormalX=0 NormalY=0 NormalZ=1 AngleXU=0 Radius=3 StartAngle=4.71239 EndAngle=7.85398
    g24: LineSegment StartX=44.5 StartY=5 StartZ=0 EndX=78.5 EndY=5 EndZ=0
    g25: LineSegment StartX=44.5 StartY=-1 StartZ=0 EndX=78.5 EndY=-1 EndZ=0
    g26: LineSegment StartX=17 StartY=-1 StartZ=0 EndX=44.5 EndY=-1 EndZ=0
    g27: LineSegment StartX=78.5 StartY=-1 StartZ=0 EndX=106 EndY=-1 EndZ=0
  constraints (67):
    c: PointOnObject(g0,g-2)
    c: Coincident(g0,g1)
    c: Horizontal(g1)
    c: Coincident(g1,g2)
    c: Coincident(g2,g3)
    c: Horizontal(g3)
    c: Vertical(g-3,g3)
    c: Horizontal(g0)
    c: Equal(g0,g1)
    c: Equal(g1,g2)
    c: Equal(g2,g3)
    c: DistanceY(g0) = 2
    c: Horizontal(g2)
    c: Tangent(g4,g6) = 1.5708
    c: Tangent(g4,g7) = -1.5708
    c: Tangent(g5,g6) = 1.5708
    c: Tangent(g5,g7) = -1.5708
    c: Equal(g4,g5)
    c: PointOnObject(g5,g0)
    c: Symmetric(g4,g5,g-2)
    c: Radius(g5) = 3
    c: PointOnObject(g8,g4)
    c: PointOnObject(g9,g5)
    c: Horizontal(g9,g8)
    c: Horizontal(g8,g0)
    c: DistanceX(g8,g9) = 40
    c: Tangent(g10,g12) = 1.5708
    c: Tangent(g10,g13) = -1.5708
    c: Tangent(g11,g12) = 1.5708
    c: Tangent(g11,g13) = -1.5708
    c: Equal(g10,g11)
    c: Tangent(g14,g16) = 1.5708
    c: Tangent(g14,g17) = -1.5708
    c: Tangent(g15,g16) = 1.5708
    c: Tangent(g15,g17) = -1.5708
    c: Equal(g14,g15)
    c: Tangent(g18,g20) = 1.5708
    c: Tangent(g18,g21) = -1.5708
    c: Tangent(g19,g20) = 1.5708
    c: Tangent(g19,g21) = -1.5708
    c: Equal(g18,g19)
    c: Tangent(g22,g24) = 1.5708
    c: Tangent(g22,g25) = -1.5708
    c: Tangent(g23,g24) = 1.5708
    c: Tangent(g23,g25) = -1.5708
    c: Equal(g22,g23)
    c: Horizontal(g14,g15)
    c: Horizontal(g18,g19)
    c: Horizontal(g22,g23)
    c: Horizontal(g10,g11)
    c: Equal(g11,g23)
    c: Equal(g23,g5)
    c: Equal(g5,g19)
    c: Equal(g19,g15)
    c: Equal(g16,g20)
    c: Equal(g20,g6)
    c: Equal(g6,g24)
    c: Equal(g12,g24)
    c: Horizontal(g10,g22)
    c: Symmetric(g19,g22,g-2)
    c: Symmetric(g10,g15,g-2)
    c: Tangent(g26,g5) = -1.5708
    c: Coincident(g26,g22)
    c: Coincident(g27,g23)
    c: Coincident(g27,g10)
    c: Equal(g26,g27)
    c: DistanceX(g11) = 140
FEATURE [Sketcher::SketchObject] Sketch054
  ExternalGeometry = -> [Sketch049]
  FullyConstrained = true
  MapMode = 5
  Placement = pos=(164.635,0,0) rot=(0.889126,0.323616,0.323616;1.68804rad)
  sketch-geometry (6):
    g0: LineSegment StartX=0.909926 StartY=78 StartZ=0 EndX=0.909926 EndY=80 EndZ=0
    g1: LineSegment StartX=0.909926 StartY=80 StartZ=0 EndX=2.90993 EndY=80 EndZ=0
    g2: LineSegment StartX=199.749 StartY=80 StartZ=0 EndX=201.749 EndY=80 EndZ=0
    g3: LineSegment StartX=201.749 StartY=80 StartZ=0 EndX=201.749 EndY=78 EndZ=0
    g4: ArcOfCircle CenterX=2.90993 CenterY=78 CenterZ=0 NormalX=0 NormalY=0 NormalZ=1 AngleXU=0 Radius=2 StartAngle=1.5708 EndAngle=3.14159
    g5: ArcOfCircle CenterX=199.749 CenterY=78 CenterZ=0 NormalX=0 NormalY=0 NormalZ=1 AngleXU=0 Radius=2 StartAngle=1.5e-15 EndAngle=1.5708
  constraints (14):
    c: Coincident(g0,g-3)
    c: Vertical(g0)
    c: Coincident(g0,g1)
    c: PointOnObject(g1,g-3)
    c: Coincident(g2,g-3)
    c: Coincident(g2,g3)
    c: Tangent(g5,g3) = 1.5708
    c: Tangent(g5,g2) = 1.5708
    c: Equal(g4,g5)
    c: Radius(g5) = 2
    c: Vertical(g3)
    c: PointOnObject(g2,g-3)
    c: Tangent(g4,g0) = 1.5708
    c: Tangent(g1,g4) = 1.5708
FEATURE [Sketcher::SketchObject] Sketch055
  ExternalGeometry = -> [Sketch052]
  FullyConstrained = true
  MapMode = 2
  Placement = pos=(-164.635,-5.7e-14,0) rot=(0.889126,-0.323616,-0.323616;1.68804rad)
  sketch-geometry (6):
    g0: ArcOfCircle CenterX=-2.90993 CenterY=78 CenterZ=0 NormalX=0 NormalY=0 NormalZ=1 AngleXU=0 Radius=2 StartAngle=6.28318 EndAngle=7.85398
    g1: ArcOfCircle CenterX=-199.749 CenterY=78 CenterZ=0 NormalX=0 NormalY=0 NormalZ=1 AngleXU=0 Radius=2 StartAngle=1.5708 EndAngle=3.14159
    g2: LineSegment StartX=-201.749 StartY=78 StartZ=0 EndX=-201.749 EndY=80 EndZ=0
    g3: LineSegment StartX=-201.749 StartY=80 StartZ=0 EndX=-199.749 EndY=80 EndZ=0
    g4: LineSegment StartX=-2.90993 StartY=80 StartZ=0 EndX=-0.909926 EndY=80 EndZ=0
    g5: LineSegment StartX=-0.909926 StartY=80 StartZ=0 EndX=-0.909926 EndY=78 EndZ=0
  constraints (15):
    c: PointOnObject(g1,g-3)
    c: Coincident(g2,g3)
    c: Vertical(g2)
    c: Tangent(g1,g2) = 1.5708
    c: Tangent(g3,g1) = 1.5708
    c: Coincident(g4,g5)
    c: Coincident(g5,g0)
    c: Tangent(g5,g0)
    c: Tangent(g0,g4) = 1.5708
    c: Coincident(g4,g-3)
    c: Equal(g0,g1)
    c: Radius(g0) = 2
    c: Coincident(g2,g-3)
    c: PointOnObject(g0,g-3)
    c: Vertical(g5)
FEATURE [Sketcher::SketchObject] Sketch056
  ExternalGeometry = -> [Sketch050]
  FullyConstrained = true
  MapMode = 5
  Placement = pos=(0,0,0) rot=(1,0,0;1.5708rad)
  sketch-geometry (6):
    g0: LineSegment StartX=161.725 StartY=80 StartZ=0 EndX=163.725 EndY=80 EndZ=0
    g1: LineSegment StartX=163.725 StartY=80 StartZ=0 EndX=163.725 EndY=78 EndZ=0
    g2: LineSegment StartX=-163.725 StartY=78 StartZ=0 EndX=-163.725 EndY=80 EndZ=0
    g3: LineSegment StartX=-163.725 StartY=80 StartZ=0 EndX=-161.725 EndY=80 EndZ=0
    g4: ArcOfCircle CenterX=-161.725 CenterY=78 CenterZ=0 NormalX=0 NormalY=0 NormalZ=1 AngleXU=0 Radius=2 StartAngle=1.5708 EndAngle=3.14159
    g5: ArcOfCircle CenterX=161.725 CenterY=78 CenterZ=0 NormalX=0 NormalY=0 NormalZ=1 AngleXU=0 Radius=2 StartAngle=-4.4e-15 EndAngle=1.5708
  constraints (14):
    c: Coincident(g0,g-3)
    c: Coincident(g0,g1)
    c: Coincident(g2,g-3)
    c: Coincident(g2,g3)
    c: Tangent(g5,g1) = 1.5708
    c: Tangent(g5,g0) = 1.5708
    c: Tangent(g4,g2) = 1.5708
    c: Tangent(g4,g3) = 1.5708
    c: Equal(g5,g4)
    c: Radius(g5) = 2
    c: PointOnObject(g3,g-3)
    c: Vertical(g2)
    c: PointOnObject(g0,g-3)
    c: Vertical(g1)
FEATURE [Sketcher::SketchObject] Sketch059
  ExternalGeometry = -> [Sketch045]
  FullyConstrained = true
  MapMode = 5
  Placement = pos=(0,0,0) rot=(0.57735,0.57735,0.57735;2.0944rad)
  sketch-geometry (7):
    g0: ArcOfCircle CenterX=132.281 CenterY=18.3274 CenterZ=0 NormalX=0 NormalY=0 NormalZ=1 AngleXU=0 Radius=2 StartAngle=5e-16 EndAngle=1.72345
    g1: ArcOfCircle CenterX=132.281 CenterY=18.3274 CenterZ=0 NormalX=0 NormalY=0 NormalZ=1 AngleXU=0 Radius=2.5 StartAngle=4.587e-13 EndAngle=1.72345
    g2: LineSegment StartX=131.977 StartY=20.3041 StartZ=0 EndX=131.901 EndY=20.7983 EndZ=0
    g3: LineSegment StartX=134.281 StartY=18.3274 StartZ=0 EndX=134.281 EndY=10.8274 EndZ=0
    g4: LineSegment StartX=134.281 StartY=10.8274 StartZ=0 EndX=134.781 EndY=10.8274 EndZ=0
    g5: LineSegment StartX=134.781 StartY=10.8274 StartZ=0 EndX=134.781 EndY=18.3274 EndZ=0
    g6: LineSegment StartX=134.781 StartY=20.8274 StartZ=0 EndX=0 EndY=20.8274 EndZ=0
  constraints (19):
    c: Coincident(g1,g0)
    c: Coincident(g2,g1)
    c: Vertical(g3)
    c: Coincident(g4,g3)
    c: Horizontal(g4)
    c: Coincident(g5,g4)
    c: Vertical(g5)
    c: Tangent(g0,g-3) = 1.5708
    c: Perpendicular(g2,g-3)
    c: Distance(g2) = 0.5
    c: Coincident(g2,g0)
    c: Radius(g0) = 2
    c: Horizontal(g6)
    c: Tangent(g6,g1)
    c: PointOnObject(g6,g-2)
    c: PointOnObject(g6,g5)
    c: Tangent(g3,g0) = 1.5708
    c: DistanceY(g4,g6) = 10
    c: Tangent(g5,g1) = -1.5708
FEATURE [Sketcher::SketchObject] Sketch060
  ExternalGeometry = -> [Sketch059]
  FullyConstrained = true
  MapMode = 5
  Placement = pos=(0,0,0) rot=(1,0,0;1.5708rad)
  expr: Constraints[5] = <<sink_plane_sketch>>.Constraints.end / 2
  sketch-geometry (3):
    g0: ArcOfCircle CenterX=315.576 CenterY=12.8274 CenterZ=0 NormalX=0 NormalY=0 NormalZ=1 AngleXU=0 Radius=2 StartAngle=4.71239 EndAngle=6.28318
    g1: LineSegment StartX=315.576 StartY=10.8274 StartZ=0 EndX=317.576 EndY=10.8274 EndZ=0
    g2: LineSegment StartX=317.576 StartY=10.8274 StartZ=0 EndX=317.576 EndY=12.8274 EndZ=0
  constraints (9):
    c: Coincident(g1,g2)
    c: Coincident(g2,g0)
    c: Tangent(g2,g0)
    c: Vertical(g2)
    c: Horizontal(g1)
    c: DistanceX(g1) = 317.576
    c: Radius(g0) = 2
    c: Tangent(g0,g1) = -1.5708
    c: Horizontal(g-3,g1)
FEATURE [PartDesign::FeaturePython] SketchOnSheet  # WARN: FeaturePython — macro-defined, semantics opaque (R4)
  BaseFeature = -> Pad009
  Sketch = -> Sketch053
  Suppressed = false
  baseObject = -> Pad009 [Face14]
  kfactor = 0.5
FEATURE [PartDesign::FeaturePython] CornerRelief  # WARN: FeaturePython — macro-defined, semantics opaque (R4)
  BaseFeature = -> SketchOnSheet
  ReliefSketch = 0
  Size = 5
  SizeRatio = 1
  Suppressed = false
  XOffset = 0
  YOffset = 0
  baseObject = -> SketchOnSheet [Edge56,Edge57]
  kfactor = 0.5
FEATURE [PartDesign::FeaturePython] CornerRelief001  # WARN: FeaturePython — macro-defined, semantics opaque (R4)
  BaseFeature = -> CornerRelief
  ReliefSketch = 0
  Size = 5
  SizeRatio = 1
  Suppressed = false
  XOffset = 0
  YOffset = 0
  baseObject = -> CornerRelief [Edge17,Edge14]
  kfactor = 0.5
  expr: Size = <<CornerRelief>>.Size
FEATURE [PartDesign::Pocket] Pocket008
  BaseFeature = -> CornerRelief001
  Direction = (-0.642788,0.766044,0)
  Length = 5
  Length2 = 5
  Midplane = true
  Profile = -> Sketch054
  ReferenceAxis = -> Sketch054 [N_Axis]
  Suppressed = false
  Type = 1
FEATURE [PartDesign::Pocket] Pocket009
  BaseFeature = -> Pocket008
  Direction = (0.642788,0.766044,0)
  Length = 5
  Length2 = 5
  Midplane = true
  Profile = -> Sketch055
  ReferenceAxis = -> Sketch055 [N_Axis]
  Suppressed = false
  Type = 0
FEATURE [PartDesign::Pocket] Pocket010
  BaseFeature = -> Pocket009
  Direction = (0,1,-2e-16)
  Length = 5
  Length2 = 5
  Midplane = true
  Profile = -> Sketch056
  ReferenceAxis = -> Sketch056 [N_Axis]
  Suppressed = false
  Type = 1
FEATURE [PartDesign::Pad] Pad017
  BaseFeature = -> Pocket010
  Direction = (1,0,0)
  Length = 635.153
  Length2 = 10
  Midplane = true
  Profile = -> Sketch059
  ReferenceAxis = -> Sketch059 [N_Axis]
  Suppressed = false
  Type = 0
  expr: Length = <<sink_plane_sketch>>.Constraints.end
FEATURE [PartDesign::Pocket] Pocket011
  BaseFeature = -> Pad017
  Direction = (0,1,-2e-16)
  Length = 5
  Length2 = 5
  Midplane = true
  Profile = -> Sketch060
  ReferenceAxis = -> Sketch060 [N_Axis]
  Suppressed = false
  Type = 1
FEATURE [PartDesign::Mirrored] Mirrored002
  BaseFeature = -> Pocket011
  MirrorPlane = -> Sketch060 [V_Axis]
  Originals = -> [Pocket011]
  Suppressed = false
FEATURE [PartDesign::Boolean] Boolean011
  BaseFeature = -> Mirrored002
  Group = -> [Compound016]
  Suppressed = false
  Type = 1
  UsePlacement = true
FEATURE [PartDesign::CoordinateSystem] Local_CS017  label="sink_LCS"
  AttacherType = Attacher::AttachEngine3D
  MapMode = 5
FEATURE [PartDesign::Body] Body012  label="sink"
  Group = -> [Binder015,Local_CS,Sketch005,Sketch006,Sketch044,Local_CS001,Sketch045,Sketch046,Sketch047,Sketch048,Pad003,Pad004,Pad005,Pad006,Sketch049,Sketch050,Pad007,Pad008,Sketch051,Local_CS003,Sketch052,Pad009,Sketch053,SketchOnSheet,CornerRelief,CornerRelief001,Sketch054,Sketch055,Sketch056,Pocket008,Pocket009,Pocket010,Local_CS004,Sketch059,Pad017,Sketch060,Pocket011,Mirrored002,Boolean011,Local_CS017]
  Origin = -> Origin012
  Tip = -> Boolean011
COMPONENT P10 — recipe-attached ("bottom_composit", modeled in this document).
Construction recipe (the document's own serialized feature program — sketch geometry with constraints, then the solid features built on it; lengths are millimeters unless a unit is written):

FEATURE [PartDesign::SubShapeBinder] Binder018
  BindCopyOnChange = 0
  BindMode = 0
  ClaimChildren = true
  Context = -> Body014 [Binder018.]
  Fuse = false
  MakeFace = true
  OffsetFill = false
  OffsetIntersection = false
  OffsetJoinType = 0
  OffsetOpenResult = false
  PartialLoad = false
  Placement = pos=(0,0,0) rot=(0,-1,0;1.5708rad)
  Relative = false
  Support = -> [Sketch063]
  _Version = 2
FEATURE [PartDesign::FeaturePython] BaseBend010  # WARN: FeaturePython — macro-defined, semantics opaque (R4)
  BendSide = 0
  BendSketch = -> Binder018
  MidPlane = true
  Reverse = false
  Suppressed = false
  length = 639.126
  radius = 0.1
  thickness = 0.3
  expr: length = <<base_sketch>>.Constraints.total_width
FEATURE [Sketcher::SketchObject] Sketch067
  AttachmentOffset = pos=(319.563,0,0) rot=(0,0,1;0rad)
  FullyConstrained = true
  MapMode = 5
  Placement = pos=(319.563,0,0) rot=(0,0,1;0rad)
  expr: .AttachmentOffset.Base.x = <<BaseBend010>>.length / 2
  expr: .Constraints.length = <<Dimensions_sketch>>.Constraints.total_depth
  sketch-geometry (8):
    g0: LineSegment StartX=0 StartY=3 StartZ=0 EndX=-6 EndY=3 EndZ=0
    g1: LineSegment StartX=-6 StartY=3 StartZ=0 EndX=-6 EndY=6 EndZ=0
    g2: LineSegment StartX=-6 StartY=6 StartZ=0 EndX=-3.4 EndY=6 EndZ=0
    g3: LineSegment StartX=-3 StartY=200 StartZ=0 EndX=0 EndY=200 EndZ=0
    g4: LineSegment StartX=0 StartY=200 StartZ=0 EndX=0 EndY=3 EndZ=0
    g5: LineSegment StartX=-3.4 StartY=6 StartZ=0 EndX=-3.4 EndY=181 EndZ=0
    g6: LineSegment StartX=-3.4 StartY=181 StartZ=0 EndX=-3 EndY=181 EndZ=0
    g7: LineSegment StartX=-3 StartY=181 StartZ=0 EndX=-3 EndY=200 EndZ=0
  constraints (24):
    c: PointOnObject(g0,g-2)
    c: Horizontal(g0)
    c: Coincident(g0,g1)
    c: Vertical(g1)
    c: Coincident(g1,g2)
    c: Horizontal(g2)
    c: Coincident(g2,g5)
    c: Coincident(g7,g3)
    c: PointOnObject(g3,g-2)
    c: Coincident(g3,g4)
    c: Coincident(g4,g0)
    c: DistanceY(g0) = 3
    c: DistanceY(g0,g2) = 3
    c: DistanceX(g0,g0) = 6
    c: DistanceX(g2) = -3.4
    c: Horizontal(g3)
    c: DistanceY(g3) = 200  'length'
    c: Coincident(g5,g6)
    c: Vertical(g5)
    c: Coincident(g6,g7)
    c: Vertical(g7)
    c: Horizontal(g6)
    c: DistanceY(g5,g5) = 175  'bend_length'
    c: DistanceX(g6,g6) = 0.4
FEATURE [PartDesign::Pocket] Pocket012
  BaseFeature = -> BaseBend010
  Direction = (0,0,-1)
  Length = 5
  Length2 = 5
  Midplane = true
  Profile = -> Sketch067
  ReferenceAxis = -> Sketch067 [N_Axis]
  Suppressed = false
  Type = 1
FEATURE [Sketcher::SketchObject] Sketch068
  AttachmentOffset = pos=(319.563,0,6) rot=(0,0,1;0rad)
  FullyConstrained = true
  MapMode = 5
  Placement = pos=(319.563,0,6) rot=(0,0,1;0rad)
  expr: .AttachmentOffset.Base.x = <<Sketch067>>.AttachmentOffset.Base.x
  expr: Constraints[16] = <<Sketch067>>.Constraints.length
  expr: Constraints[23] = <<Sketch067>>.Constraints.bend_length + 6 mm
  sketch-geometry (8):
    g0: LineSegment StartX=8.3238e-12 StartY=6 StartZ=0 EndX=-9.1 EndY=6 EndZ=0
    g1: LineSegment StartX=-9.1 StartY=6 StartZ=0 EndX=-9.1 EndY=9.1 EndZ=0
    g2: LineSegment StartX=-9.1 StartY=9.1 StartZ=0 EndX=-9.1 EndY=9.1 EndZ=0
    g3: LineSegment StartX=-3 StartY=200 StartZ=0 EndX=0 EndY=200 EndZ=0
    g4: LineSegment StartX=0 StartY=200 StartZ=0 EndX=8.3238e-12 EndY=6 EndZ=0
    g5: LineSegment StartX=-9.1 StartY=9.1 StartZ=0 EndX=-9.1 EndY=181 EndZ=0
    g6: LineSegment StartX=-9.1 StartY=181 StartZ=0 EndX=-3 EndY=181 EndZ=0
    g7: LineSegment StartX=-3 StartY=181 StartZ=0 EndX=-3 EndY=200 EndZ=0
  constraints (24):
    c: PointOnObject(g0,g-2)
    c: Horizontal(g0)
    c: Coincident(g0,g1)
    c: Coincident(g1,g2)
    c: Coincident(g2,g5)
    c: Coincident(g7,g3)
    c: PointOnObject(g3,g-2)
    c: Horizontal(g3)
    c: Coincident(g3,g4)
    c: Coincident(g4,g0)
    c: DistanceX(g0,g0) = 9.1
    c: Vertical(g1)
    c: DistanceY(g0) = 6
    c: DistanceY(g1,g1) = 3.1
    c: Horizontal(g2)
    c: DistanceX(g2) = -9.1
    c: DistanceY(g3) = 200
    c: Coincident(g5,g6)
    c: Vertical(g5)
    c: Coincident(g6,g7)
    c: Vertical(g7)
    c: Horizontal(g6)
    c: DistanceX(g3,g3) = 3
    c: DistanceY(g-1,g6) = 181
FEATURE [PartDesign::Pocket] Pocket013
  BaseFeature = -> Pocket012
  Direction = (0,0,-1)
  Length = 3
  Length2 = 100
  Profile = -> Sketch068
  ReferenceAxis = -> Sketch068 [N_Axis]
  Suppressed = false
  Type = 4
FEATURE [PartDesign::Mirrored] Mirrored003
  BaseFeature = -> Pocket013
  MirrorPlane = -> YZ_Plane014
  Originals = -> [Pocket012,Pocket013]
  Suppressed = false
FEATURE [PartDesign::Boolean] Boolean013
  BaseFeature = -> Mirrored003
  Group = -> [Compound018]
  Refine = true
  Suppressed = false
  Type = 0
  UsePlacement = true
FEATURE [PartDesign::Boolean] Boolean014
  BaseFeature = -> Boolean013
  Group = -> [Compound019]
  Suppressed = false
  Type = 1
  UsePlacement = true
FEATURE [Sketcher::SketchObject] Sketch074
  AttachmentOffset = pos=(319.563,0,0) rot=(0,0,1;0rad)
  FullyConstrained = true
  MapMode = 5
  Placement = pos=(319.563,0,0) rot=(0,0,1;0rad)
  expr: .AttachmentOffset.Base.x = <<Sketch067>>.AttachmentOffset.Base.x
  sketch-geometry (4):
    g0: LineSegment StartX=0 StartY=0 StartZ=0 EndX=0 EndY=15 EndZ=0
    g1: LineSegment StartX=0 StartY=15 StartZ=0 EndX=-6 EndY=15 EndZ=0
    g2: LineSegment StartX=-6 StartY=15 StartZ=0 EndX=-6 EndY=0 EndZ=0
    g3: LineSegment StartX=-6 StartY=0 StartZ=0 EndX=0 EndY=0 EndZ=0
  constraints (11):
    c: Coincident(g0,g1)
    c: Coincident(g1,g2)
    c: Coincident(g2,g3)
    c: Coincident(g3,g0)
    c: Vertical(g0)
    c: Vertical(g2)
    c: Horizontal(g1)
    c: Horizontal(g3)
    c: Coincident(g0,g-1)
    c: DistanceY(g0) = 15
    c: DistanceX(g1) = -6
FEATURE [PartDesign::Pocket] Pocket014
  BaseFeature = -> Boolean014
  Direction = (0,0,-1)
  Length = 5
  Length2 = 5
  Midplane = true
  Profile = -> Sketch074
  ReferenceAxis = -> Sketch074 [N_Axis]
  Suppressed = false
  Type = 1
FEATURE [PartDesign::Mirrored] Mirrored004
  BaseFeature = -> Pocket014
  MirrorPlane = -> YZ_Plane014
  Originals = -> [Pocket014]
  Suppressed = false
FEATURE [PartDesign::CoordinateSystem] Local_CS018  label="bottom_composit_LCS"
  AttacherType = Attacher::AttachEngine3D
  AttachmentSupport = -> [XY_Plane014]
  MapMode = 5
FEATURE [PartDesign::CoordinateSystem] Local_CS022  label="bottom_composit_basin_LCS"
  AttacherType = Attacher::AttachEngine3D
  AttachmentOffset = pos=(0,108,11) rot=(0,0,1;0rad)
  AttachmentSupport = -> [XY_Plane014]
  MapMode = 5
  Placement = pos=(0,108,11) rot=(0,0,1;0rad)
  expr: .AttachmentOffset.Base.z = 11 mm
FEATURE [PartDesign::CoordinateSystem] Local_CS023  label="bottom_composit_rails_LCS"
  AttacherType = Attacher::AttachEngine3D
  AttachmentOffset = pos=(200,9,6) rot=(0,0,1;1.5708rad)
  AttachmentSupport = -> [XY_Plane014]
  MapMode = 5
  Placement = pos=(200,9,6) rot=(0,0,1;1.5708rad)
  expr: AttachmentOffset = <<LinearArray010>>.Placement
FEATURE [PartDesign::CoordinateSystem] Local_CS030  label="bottom_composit_shield_LCS"
  AttacherType = Attacher::AttachEngine3D
  AttachmentOffset = pos=(0,203,6) rot=(0,0,1;0rad)
  AttachmentSupport = -> [XY_Plane014]
  MapMode = 5
  Placement = pos=(0,203,6) rot=(0,0,1;0rad)
  expr: .AttachmentOffset.Base.y = <<Dimensions_sketch>>.Constraints.total_depth + 3 mm
FEATURE [PartDesign::Body] Body014  label="bottom_composit"
  Group = -> [Binder018,BaseBend010,Sketch067,Pocket012,Sketch068,Pocket013,Mirrored003,Boolean013,Boolean014,Sketch074,Pocket014,Mirrored004,Local_CS018,Local_CS022,Local_CS023,Local_CS030]
  Origin = -> Origin014
  Tip = -> Mirrored004
COMPONENT P11 — recipe-attached ("Body", modeled in this document).
Construction recipe (the document's own serialized feature program — sketch geometry with constraints, then the solid features built on it; lengths are millimeters unless a unit is written):

FEATURE [Sketcher::SketchObject] Sketch071
  AttachmentOffset = pos=(0,-6,0) rot=(0,0,1;0rad)
  FullyConstrained = true
  MapMode = 5
  Placement = pos=(0,-1e-15,-6) rot=(1,0,0;1.5708rad)
  sketch-geometry (6):
    g0: LineSegment StartX=0 StartY=0 StartZ=0 EndX=4 EndY=0 EndZ=0
    g1: LineSegment StartX=4 StartY=0 StartZ=0 EndX=4 EndY=3 EndZ=0
    g2: LineSegment StartX=4 StartY=3 StartZ=0 EndX=1.7 EndY=3 EndZ=0
    g3: LineSegment StartX=1.7 StartY=3 StartZ=0 EndX=1.7 EndY=6 EndZ=0
    g4: LineSegment StartX=1.7 StartY=6 StartZ=0 EndX=0 EndY=6 EndZ=0
    g5: LineSegment StartX=0 StartY=6 StartZ=0 EndX=0 EndY=0 EndZ=0
  constraints (17):
    c: Coincident(g-1,g0)
    c: Horizontal(g0)
    c: Coincident(g0,g1)
    c: Vertical(g1)
    c: Coincident(g1,g2)
    c: Horizontal(g2)
    c: Coincident(g2,g3)
    c: Vertical(g3)
    c: Coincident(g3,g4)
    c: PointOnObject(g4,g-2)
    c: Horizontal(g4)
    c: Coincident(g4,g5)
    c: Coincident(g5,g0)
    c: DistanceY(g1) = 3
    c: DistanceY(g4) = 6
    c: DistanceX(g3) = 1.7
    c: DistanceX(g0) = 4
FEATURE [PartDesign::Revolution] Revolution
  Angle = 360
  Angle2 = 60
  Axis = (0,2e-16,1)
  Base = (0,-1.3e-15,-6)
  Placement = pos=(0,0,0) rot=(1,0,0;1.5708rad)
  Profile = -> Sketch071
  ReferenceAxis = -> Sketch071 [V_Axis]
  Reversed = true
  Suppressed = false
  Type = 0
FEATURE [PartDesign::Body] Body015  label="Body"
  Group = -> [Sketch071,Revolution]
  Origin = -> Origin015
  Tip = -> Revolution
COMPONENT P12 — recipe-attached ("rail", modeled in this document).
Construction recipe (the document's own serialized feature program — sketch geometry with constraints, then the solid features built on it; lengths are millimeters unless a unit is written):

FEATURE [PartDesign::SubShapeBinder] Binder019
  BindCopyOnChange = 0
  BindMode = 0
  ClaimChildren = true
  Context = -> Body016 [Binder019.]
  Fuse = false
  MakeFace = true
  OffsetFill = false
  OffsetIntersection = false
  OffsetJoinType = 0
  OffsetOpenResult = false
  PartialLoad = false
  Relative = false
  Support = -> [Sketch070]
  _Version = 2
FEATURE [PartDesign::Pad] Pad018
  Direction = (0,0,1)
  Length = 5
  Length2 = 10
  Profile = -> Binder019
  Suppressed = false
  Type = 0
FEATURE [PartDesign::Boolean] Boolean015
  BaseFeature = -> Pad018
  Group = -> [Compound020]
  Suppressed = false
  Type = 1
  UsePlacement = true
FEATURE [PartDesign::CoordinateSystem] Local_CS024  label="rails_LCS"
  AttacherType = Attacher::AttachEngine3D
  AttachmentSupport = -> [XY_Plane016]
  MapMode = 5
FEATURE [PartDesign::Body] Body016  label="rail"
  Group = -> [Binder019,Pad018,Boolean015,Local_CS024]
  Origin = -> Origin016
  Tip = -> Boolean015
COMPONENT P13 — recipe-attached ("Body017", modeled in this document).
Construction recipe (the document's own serialized feature program — sketch geometry with constraints, then the solid features built on it; lengths are millimeters unless a unit is written):

FEATURE [Sketcher::SketchObject] Sketch072
  FullyConstrained = true
  MapMode = 5
  Placement = pos=(0,0,0) rot=(1,0,0;1.5708rad)
  sketch-geometry (6):
    g0: LineSegment StartX=0 StartY=0 StartZ=0 EndX=1.7 EndY=0 EndZ=0
    g1: LineSegment StartX=1.7 StartY=0 StartZ=0 EndX=1.7 EndY=2.5 EndZ=0
    g2: LineSegment StartX=1.7 StartY=2.5 StartZ=0 EndX=4 EndY=2.5 EndZ=0
    g3: LineSegment StartX=4 StartY=2.5 StartZ=0 EndX=4 EndY=5 EndZ=0
    g4: LineSegment StartX=4 StartY=5 StartZ=0 EndX=0 EndY=5 EndZ=0
    g5: LineSegment StartX=0 StartY=5 StartZ=0 EndX=0 EndY=0 EndZ=0
  constraints (17):
    c: Coincident(g-1,g0)
    c: PointOnObject(g0,g-1)
    c: Coincident(g0,g1)
    c: Vertical(g1)
    c: Coincident(g1,g2)
    c: Horizontal(g2)
    c: Coincident(g2,g3)
    c: Vertical(g3)
    c: Coincident(g3,g4)
    c: Horizontal(g4)
    c: Coincident(g4,g5)
    c: Coincident(g5,g0)
    c: Vertical(g5)
    c: DistanceX(g0) = 1.7
    c: DistanceY(g5,g5) = 5
    c: DistanceY(g1,g1) = 2.5
    c: DistanceX(g4,g4) = 4
FEATURE [PartDesign::Revolution] Revolution001
  Angle = 360
  Angle2 = 60
  Axis = (0,2e-16,1)
  Base = (0,0,0)
  Placement = pos=(0,0,0) rot=(1,0,0;1.5708rad)
  Profile = -> Sketch072
  ReferenceAxis = -> Sketch072 [V_Axis]
  Reversed = true
  Suppressed = false
  Type = 0
FEATURE [PartDesign::Body] Body017
  Group = -> [Sketch072,Revolution001]
  Origin = -> Origin017
  Tip = -> Revolution001
COMPONENT P14 — recipe-attached ("electric_shield", modeled in this document).
Construction recipe (the document's own serialized feature program — sketch geometry with constraints, then the solid features built on it; lengths are millimeters unless a unit is written):

FEATURE [PartDesign::SubShapeBinder] Binder021
  BindCopyOnChange = 0
  BindMode = 0
  ClaimChildren = true
  Context = -> Body018 [Binder021.]
  Fuse = false
  MakeFace = true
  OffsetFill = false
  OffsetIntersection = false
  OffsetJoinType = 0
  OffsetOpenResult = false
  PartialLoad = false
  Relative = false
  Support = -> [Offset2D001]
  _Version = 2
FEATURE [PartDesign::FeaturePython] BaseBend015  # WARN: FeaturePython — macro-defined, semantics opaque (R4)
  BendSide = 0
  BendSketch = -> Binder021
  MidPlane = false
  Reverse = true
  Suppressed = false
  length = 100
  radius = 0.1
  thickness = 0.3
FEATURE [PartDesign::FeaturePython] Bend008  # WARN: FeaturePython — macro-defined, semantics opaque (R4)
  AutoMiter = false
  BaseFeature = -> BaseBend015
  BendType = 1
  LengthList = [30]
  LengthSpec = 1
  ReliefFactor = 0.7
  Suppressed = false
  UseReliefFactor = false
  angle = 90
  baseObject = -> BaseBend015 [Edge4,Edge7,Edge10,Edge12]
  bendAList = [90]
  extend1 = 0
  extend2 = 0
  gap1 = 0
  gap2 = 0
  invert = true
  kfactor = 0.5
  length = 30
  maxExtendDist = 5
  minGap = 0.2
  minReliefGap = 1
  miterangle1 = 0
  miterangle2 = 0
  offset = 0
  radius = 0.1
  reliefType = 0
  reliefd = 1
  reliefw = 0.8
  sketchflip = false
  sketchinvert = false
  unfold = false
  expr: radius = BaseBend015.radius
FEATURE [PartDesign::CoordinateSystem] Local_CS019
  AttacherType = Attacher::AttachEngine3D
  AttachmentOffset = pos=(0,0,33) rot=(0,0,1;0rad)
  AttachmentSupport = -> [XY_Plane018]
  MapMode = 5
  Placement = pos=(0,0,33) rot=(0,0,1;0rad)
  expr: .AttachmentOffset.Base.z = <<Bend008>>.length + 3 mm
FEATURE [Sketcher::SketchObject] Sketch105
  AttachmentSupport = -> [XY_Plane018]
  FullyConstrained = true
  MapMode = 5
  sketch-geometry (5):
    g0: Circle CenterX=25 CenterY=-140 CenterZ=0 NormalX=0 NormalY=0 NormalZ=1 AngleXU=0 Radius=11.85
    g1: Circle CenterX=25 CenterY=-90 CenterZ=0 NormalX=0 NormalY=0 NormalZ=1 AngleXU=0 Radius=11.85
    g2: Circle CenterX=25 CenterY=-40 CenterZ=0 NormalX=0 NormalY=0 NormalZ=1 AngleXU=0 Radius=11.85
    g3: LineSegment StartX=25 StartY=-140 StartZ=0 EndX=25 EndY=-90 EndZ=0
    g4: LineSegment StartX=25 StartY=-90 StartZ=0 EndX=25 EndY=-40 EndZ=0
  constraints (13):
    c: Coincident(g3,g0)
    c: Coincident(g3,g1)
    c: Coincident(g3,g4)
    c: Coincident(g4,g2)
    c: Vertical(g3)
    c: Vertical(g4)
    c: Equal(g0,g1)
    c: Equal(g0,g2)
    c: Diameter(g0) = 23.7  'r'
    c: Equal(g3,g4)
    c: DistanceY(g3,g3) = 50
    c: DistanceX(g0) = 25
    c: DistanceY(g0) = -140
FEATURE [PartDesign::Pocket] Pocket019
  BaseFeature = -> Bend008
  Direction = (0,0,-1)
  Length = 5
  Length2 = 5
  Midplane = true
  Profile = -> Sketch105
  ReferenceAxis = -> Sketch105 [N_Axis]
  Suppressed = false
  Type = 1
FEATURE [PartDesign::SubShapeBinder] Binder036
  BindCopyOnChange = 0
  BindMode = 0
  ClaimChildren = true
  Context = -> <external composit_stand9_model.FCStd>#Assembly [electric_shield.Binder036.]
  Fuse = false
  MakeFace = true
  OffsetFill = false
  OffsetIntersection = false
  OffsetJoinType = 0
  OffsetOpenResult = false
  PartialLoad = false
  Placement = pos=(-20,-70,0) rot=(0,0,1;0rad)
  Relative = false
  Support = -> [<external UET-VAF-060A67.FCStd>#Sketch]
  _Version = 2
FEATURE [PartDesign::Pocket] Pocket020
  BaseFeature = -> Pocket019
  Direction = (0,0,-1)
  Length = 5
  Length2 = 5
  Midplane = true
  Profile = -> Binder036
  Suppressed = false
  Type = 1
FEATURE [PartDesign::Boolean] Boolean016
  BaseFeature = -> Pocket020
  Group = -> [Compound024]
  Suppressed = false
  Type = 1
  UsePlacement = true
FEATURE [PartDesign::CoordinateSystem] Local_CS033
  AttacherType = Attacher::AttachEngine3D
  AttachmentOffset = pos=(0,0,3) rot=(0,0,1;0rad)
  AttachmentSupport = -> [Sketch105]
  MapMode = 11
  Placement = pos=(25,-40,-3) rot=(0.707107,-0.707107,0;3.14159rad)
FEATURE [PartDesign::CoordinateSystem] Local_CS034
  AttacherType = Attacher::AttachEngine3D
  AttachmentOffset = pos=(0,0,3) rot=(0,0,1;0rad)
  AttachmentSupport = -> [Sketch105]
  MapMode = 11
  Placement = pos=(25,-90,-3) rot=(0.707107,-0.707107,0;3.14159rad)
FEATURE [PartDesign::CoordinateSystem] Local_CS035
  AttacherType = Attacher::AttachEngine3D
  AttachmentOffset = pos=(0,0,3) rot=(0,0,1;0rad)
  AttachmentSupport = -> [Sketch105]
  MapMode = 11
  Placement = pos=(25,-140,-3) rot=(0.707107,-0.707107,0;3.14159rad)
FEATURE [PartDesign::Body] Body018  label="electric_shield"
  Group = -> [Binder021,BaseBend015,Bend008,Sketch105,Pocket019,Binder036,Pocket020,Local_CS033,Local_CS034,Local_CS035,Boolean016,Local_CS019]
  Origin = -> Origin018
  Tip = -> Boolean016
COMPONENT P15 — recipe-attached ("magnet_fix", modeled in this document).
Construction recipe (the document's own serialized feature program — sketch geometry with constraints, then the solid features built on it; lengths are millimeters unless a unit is written):

FEATURE [PartDesign::SubShapeBinder] Binder022
  BindCopyOnChange = 0
  BindMode = 0
  ClaimChildren = true
  Context = -> Body019 [Binder022.]
  Fuse = false
  MakeFace = true
  OffsetFill = false
  OffsetIntersection = false
  OffsetJoinType = 0
  OffsetOpenResult = false
  PartialLoad = false
  Relative = false
  Support = -> [Sketch076]
  _Version = 2
FEATURE [PartDesign::Pad] Pad019
  Direction = (0,0,1)
  Length = 41.3
  Length2 = 10
  Profile = -> Binder022
  Suppressed = false
  Type = 0
  expr: Length = <<magnet_fix>>#<<Properties>>.length
FEATURE [PartDesign::Fillet] Fillet
  Base = -> Pad019 [Edge1,Edge2,Edge3,Edge4,Edge5,Edge6,Edge7,Edge8,Edge9]
  BaseFeature = -> Pad019
  Radius = 2
  SupportTransform = false
  Suppressed = false
  UseAllEdges = true
FEATURE [PartDesign::Boolean] Boolean018
  BaseFeature = -> Fillet
  Group = -> [Compound026]
  Suppressed = false
  Type = 1
  UsePlacement = true
FEATURE [PartDesign::CoordinateSystem] Local_CS026  label="magnet_fix_LCS"
  AttacherType = Attacher::AttachEngine3D
  AttachmentSupport = -> [XY_Plane019]
  MapMode = 5
FEATURE [PartDesign::CoordinateSystem] Local_CS028
  AttacherType = Attacher::AttachEngine3D
  AttachmentOffset = pos=(-7.3,20,0) rot=(0.707107,0.707107,0;3.14159rad)
  AttachmentSupport = -> [YZ_Plane019]
  MapMode = 5
  Placement = pos=(0,-7.3,20) rot=(0,1,0;4.71239rad)
FEATURE [PartDesign::Body] Body019  label="magnet_fix"
  Group = -> [Binder022,Pad019,Fillet,Boolean018,Local_CS026,Local_CS028]
  Origin = -> Origin019
  Tip = -> Boolean018
COMPONENT P16 — recipe-attached ("Body020", modeled in this document).
Construction recipe (the document's own serialized feature program — sketch geometry with constraints, then the solid features built on it; lengths are millimeters unless a unit is written):

FEATURE [Sketcher::SketchObject] Sketch077
  FullyConstrained = true
  MapMode = 5
  Placement = pos=(0,0,0) rot=(1,0,0;1.5708rad)
  sketch-geometry (6):
    g0: LineSegment StartX=0 StartY=20 StartZ=0 EndX=4 EndY=20 EndZ=0
    g1: LineSegment StartX=4 StartY=20 StartZ=0 EndX=4 EndY=3 EndZ=0
    g2: LineSegment StartX=4 StartY=3 StartZ=0 EndX=1.7 EndY=3 EndZ=0
    g3: LineSegment StartX=1.7 StartY=3 StartZ=0 EndX=1.7 EndY=-3 EndZ=0
    g4: LineSegment StartX=1.7 StartY=-3 StartZ=0 EndX=0 EndY=-3 EndZ=0
    g5: LineSegment StartX=0 StartY=-3 StartZ=0 EndX=0 EndY=20 EndZ=0
  constraints (18):
    c: PointOnObject(g0,g-2)
    c: Horizontal(g0)
    c: Coincident(g0,g1)
    c: Vertical(g1)
    c: Coincident(g1,g2)
    c: Horizontal(g2)
    c: Coincident(g2,g3)
    c: Vertical(g3)
    c: Coincident(g3,g4)
    c: PointOnObject(g4,g-2)
    c: Horizontal(g4)
    c: Coincident(g4,g5)
    c: Coincident(g5,g0)
    c: DistanceY(g4) = -3
    c: DistanceX(g3) = 1.7
    c: DistanceY(g2) = 3
    c: DistanceX(g1) = 4
    c: DistanceY(g0) = 20
FEATURE [PartDesign::Revolution] Revolution002
  Angle = 360
  Angle2 = 60
  Axis = (0,2e-16,1)
  Base = (0,0,0)
  Placement = pos=(0,0,0) rot=(1,0,0;1.5708rad)
  Profile = -> Sketch077
  ReferenceAxis = -> Sketch077 [V_Axis]
  Reversed = true
  Suppressed = false
  Type = 0
FEATURE [PartDesign::Body] Body020
  Group = -> [Sketch077,Revolution002]
  Origin = -> Origin020
  Tip = -> Revolution002
COMPONENT P17 — recipe-attached ("front_shield", modeled in this document).
Construction recipe (the document's own serialized feature program — sketch geometry with constraints, then the solid features built on it; lengths are millimeters unless a unit is written):

FEATURE [PartDesign::SubShapeBinder] Binder024
  BindCopyOnChange = 0
  BindMode = 0
  ClaimChildren = true
  Context = -> Body021 [Binder024.]
  Fuse = false
  MakeFace = true
  OffsetFill = false
  OffsetIntersection = false
  OffsetJoinType = 0
  OffsetOpenResult = false
  PartialLoad = false
  Relative = false
  Support = -> [Connect010]
  _Version = 2
FEATURE [PartDesign::FeaturePython] BaseBend016  # WARN: FeaturePython — macro-defined, semantics opaque (R4)
  BendSide = 0
  BendSketch = -> Binder024
  MidPlane = false
  Reverse = false
  Suppressed = false
  length = 130
  radius = 1
  thickness = 1
FEATURE [PartDesign::FeaturePython] Extend003  # WARN: FeaturePython — macro-defined, semantics opaque (R4)
  BaseFeature = -> BaseBend016
  Offset = 0.02
  Refine = true
  Suppressed = false
  UseSubtraction = false
  baseObject = -> BaseBend016 [Face1]
  gap1 = 0
  gap2 = 0
  length = 0
FEATURE [PartDesign::CoordinateSystem] Local_CS029
  AttacherType = Attacher::AttachEngine3D
  AttachmentSupport = -> [XY_Plane021]
  MapMode = 5
FEATURE [Sketcher::SketchObject] Sketch084
  FullyConstrained = true
  MapMode = 5
  Placement = pos=(0,0,0) rot=(1,0,0;1.5708rad)
  sketch-geometry (5):
    g0: LineSegment StartX=-320 StartY=1 StartZ=0 EndX=-320 EndY=0 EndZ=0
    g1: LineSegment StartX=-320 StartY=0 StartZ=0 EndX=320 EndY=0 EndZ=0
    g2: LineSegment StartX=320 StartY=0 StartZ=0 EndX=320 EndY=1 EndZ=0
    g3: LineSegment StartX=320 StartY=1 StartZ=0 EndX=-320 EndY=1 EndZ=0
    g4: GeomPoint X=0 Y=0.5 Z=0
  constraints (13):
    c: Coincident(g0,g1)
    c: Coincident(g1,g2)
    c: Coincident(g2,g3)
    c: Coincident(g3,g0)
    c: Vertical(g0)
    c: Vertical(g2)
    c: Horizontal(g1)
    c: Horizontal(g3)
    c: Symmetric(g2,g0,g4)
    c: PointOnObject(g4,g-2)
    c: PointOnObject(g1,g-1)
    c: DistanceX(g1,g1) = 640
    c: DistanceY(g2,g2) = 1
FEATURE [Sketcher::SketchObject] Sketch085
  AttachmentSupport = -> [XZ_Plane021]
  FullyConstrained = true
  MapMode = 5
  Placement = pos=(0,0,0) rot=(1,0,0;1.5708rad)
  sketch-geometry (5):
    g0: LineSegment StartX=-268.5 StartY=0 StartZ=0 EndX=268.5 EndY=0 EndZ=0
    g1: LineSegment StartX=268.5 StartY=0 StartZ=0 EndX=268.5 EndY=3 EndZ=0
    g2: LineSegment StartX=268.5 StartY=3 StartZ=0 EndX=-268.5 EndY=3 EndZ=0
    g3: LineSegment StartX=-268.5 StartY=3 StartZ=0 EndX=-268.5 EndY=0 EndZ=0
    g4: GeomPoint X=0 Y=1.5 Z=0
  constraints (13):
    c: Coincident(g0,g1)
    c: Coincident(g1,g2)
    c: Coincident(g2,g3)
    c: Coincident(g3,g0)
    c: Horizontal(g0)
    c: Horizontal(g2)
    c: Vertical(g1)
    c: Vertical(g3)
    c: Symmetric(g2,g0,g4)
    c: PointOnObject(g4,g-2)
    c: PointOnObject(g0,g-1)
    c: DistanceY(g1,g1) = 3
    c: DistanceX(g0,g0) = 537
FEATURE [PartDesign::Pocket] Pocket015
  BaseFeature = -> Extend003
  Direction = (0,1,-2e-16)
  Length = 5
  Length2 = 5
  Midplane = true
  Profile = -> Sketch084
  ReferenceAxis = -> Sketch084 [N_Axis]
  Suppressed = false
  Type = 1
FEATURE [PartDesign::Pocket] Pocket016
  BaseFeature = -> Pocket015
  Direction = (0,1,-2e-16)
  Length = 5
  Length2 = 5
  Midplane = true
  Profile = -> Sketch085
  ReferenceAxis = -> Sketch085 [N_Axis]
  Suppressed = false
  Type = 1
FEATURE [PartDesign::Boolean] Boolean031
  BaseFeature = -> Pocket016
  Group = -> [Compound027]
  Suppressed = false
  Type = 1
  UsePlacement = false
FEATURE [PartDesign::Body] Body021  label="front_shield"
  Group = -> [Binder024,BaseBend016,Extend003,Sketch084,Sketch085,Pocket015,Pocket016,Boolean031,Local_CS029]
  Origin = -> Origin021
  Placement = pos=(0,183,11) rot=(0,0,1;0rad)
  Tip = -> Boolean031
COMPONENT P18 — recipe-attached ("basin", modeled in this document).
Construction recipe (the document's own serialized feature program — sketch geometry with constraints, then the solid features built on it; lengths are millimeters unless a unit is written):

FEATURE [PartDesign::SubShapeBinder] Binder025
  BindCopyOnChange = 0
  BindMode = 0
  ClaimChildren = true
  Context = -> Body022 [Binder025.]
  Fuse = false
  MakeFace = true
  OffsetFill = false
  OffsetIntersection = false
  OffsetJoinType = 0
  OffsetOpenResult = false
  PartialLoad = false
  Placement = pos=(0,0,100) rot=(0,0,1;0rad)
  Relative = false
  Support = -> [Sketch081]
  _Version = 2
FEATURE [PartDesign::Pad] Pad020
  Direction = (0,0,1)
  Length = 5
  Length2 = 10
  Placement = pos=(0,0,100) rot=(0,0,1;0rad)
  Profile = -> Binder025 [Face1]
  Reversed = true
  Suppressed = false
  Type = 0
FEATURE [PartDesign::SubShapeBinder] Binder026
  BindCopyOnChange = 0
  BindMode = 0
  ClaimChildren = true
  Context = -> Body022 [Binder026.]
  Fuse = false
  MakeFace = true
  OffsetFill = false
  OffsetIntersection = false
  OffsetJoinType = 0
  OffsetOpenResult = false
  PartialLoad = false
  Placement = pos=(0,0,70) rot=(0,0,1;0rad)
  Relative = true
  Support = -> [Sketch082]
  _Version = 2
FEATURE [PartDesign::Pad] Pad021
  BaseFeature = -> Pad020
  Direction = (0,0,1)
  Length = 30
  Length2 = 10
  Placement = pos=(0,0,100) rot=(0,0,1;0rad)
  Profile = -> Binder026
  Suppressed = false
  Type = 0
FEATURE [PartDesign::CoordinateSystem] Local_CS021  label="basin_LCS"
  AttacherType = Attacher::AttachEngine3D
  AttachmentSupport = -> [XY_Plane022]
  MapMode = 5
FEATURE [PartDesign::SubShapeBinder] Binder027
  BindCopyOnChange = 0
  BindMode = 0
  ClaimChildren = true
  Context = -> Body022 [Binder027.]
  Fuse = false
  MakeFace = true
  OffsetFill = false
  OffsetIntersection = false
  OffsetJoinType = 0
  OffsetOpenResult = false
  PartialLoad = false
  Relative = false
  Support = -> [Sketch083]
  _Version = 2
FEATURE [PartDesign::AdditiveLoft] AdditiveLoft
  BaseFeature = -> Pad021
  Closed = false
  Placement = pos=(0,0,100) rot=(0,0,1;0rad)
  Profile = -> Binder027 [Face1]
  Ruled = false
  Sections = -> [Binder026]
  Suppressed = false
FEATURE [PartDesign::Body] Body022  label="basin"
  Group = -> [Binder025,Pad020,Binder026,Pad021,Local_CS021,Binder027,AdditiveLoft]
  Origin = -> Origin022
  Tip = -> AdditiveLoft
COMPONENT P19 — recipe-attached ("Body024", modeled in this document).
Construction recipe (the document's own serialized feature program — sketch geometry with constraints, then the solid features built on it; lengths are millimeters unless a unit is written):

FEATURE [PartDesign::SubShapeBinder] Binder030
  BindCopyOnChange = 0
  BindMode = 0
  ClaimChildren = true
  Context = -> Body024 [Binder030.]
  Fuse = false
  MakeFace = true
  OffsetFill = false
  OffsetIntersection = false
  OffsetJoinType = 0
  OffsetOpenResult = false
  PartialLoad = false
  Relative = false
  Support = -> [Connect011]
  _Version = 2
FEATURE [PartDesign::Pad] Pad022
  Direction = (0,0,1)
  Length = 3
  Length2 = 10
  Profile = -> Binder030
  Refine = true
  Suppressed = false
  Type = 0
FEATURE [PartDesign::CoordinateSystem] Local_CS031
  AttacherType = Attacher::AttachEngine3D
  AttachmentSupport = -> [XY_Plane025]
  MapMode = 5
FEATURE [PartDesign::Body] Body024
  Group = -> [Binder030,Pad022,Local_CS031]
  Origin = -> Origin025
  Tip = -> Pad022
COMPONENT P20 — recipe-attached ("Body025", modeled in this document).
Construction recipe (the document's own serialized feature program — sketch geometry with constraints, then the solid features built on it; lengths are millimeters unless a unit is written):

FEATURE [PartDesign::SubShapeBinder] Binder031
  BindCopyOnChange = 0
  BindMode = 0
  ClaimChildren = true
  Context = -> Body025 [Binder031.]
  Fuse = false
  MakeFace = true
  OffsetFill = false
  OffsetIntersection = false
  OffsetJoinType = 0
  OffsetOpenResult = false
  PartialLoad = false
  Relative = false
  Support = -> [Connect012]
  _Version = 2
FEATURE [PartDesign::Pad] Pad023
  Direction = (0,0,1)
  Length = 5
  Length2 = 10
  Profile = -> Binder031
  Suppressed = false
  Type = 0
FEATURE [PartDesign::Body] Body025
  Group = -> [Binder031,Pad023]
  Origin = -> Origin026
  Tip = -> Pad023
COMPONENT P21 — recipe-attached ("bottom_fix_back", modeled in this document).
Construction recipe (the document's own serialized feature program — sketch geometry with constraints, then the solid features built on it; lengths are millimeters unless a unit is written):

FEATURE [PartDesign::SubShapeBinder] Binder032
  BindCopyOnChange = 0
  BindMode = 0
  ClaimChildren = true
  Context = -> Body026 [Binder032.]
  Fuse = false
  MakeFace = true
  OffsetFill = false
  OffsetIntersection = false
  OffsetJoinType = 0
  OffsetOpenResult = false
  PartialLoad = false
  Relative = false
  Support = -> [Sketch095]
  _Version = 2
FEATURE [PartDesign::FeaturePython] BaseBend021  # WARN: FeaturePython — macro-defined, semantics opaque (R4)
  BendSide = 0
  BendSketch = -> Binder032
  MidPlane = true
  Reverse = false
  Suppressed = false
  length = 100
  radius = 0.1
  thickness = 0.3
FEATURE [PartDesign::Boolean] Boolean034
  BaseFeature = -> BaseBend021
  Group = -> [Compound031]
  Suppressed = false
  Type = 1
  UsePlacement = true
FEATURE [PartDesign::Body] Body026  label="bottom_fix_back"
  Group = -> [Binder032,BaseBend021,Boolean034]
  Origin = -> Origin027
  Tip = -> Boolean034
COMPONENT P22 — recipe-attached ("Body027", modeled in this document).
Construction recipe (the document's own serialized feature program — sketch geometry with constraints, then the solid features built on it; lengths are millimeters unless a unit is written):

FEATURE [Sketcher::SketchObject] Sketch096
  FullyConstrained = true
  MapMode = 5
  Placement = pos=(0,0,0) rot=(0.57735,0.57735,0.57735;2.0944rad)
  sketch-geometry (6):
    g0: LineSegment StartX=0 StartY=0 StartZ=0 EndX=0 EndY=8 EndZ=0
    g1: LineSegment StartX=0 StartY=8 StartZ=0 EndX=4 EndY=8 EndZ=0
    g2: LineSegment StartX=4 StartY=8 StartZ=0 EndX=4 EndY=6 EndZ=0
    g3: LineSegment StartX=4 StartY=6 StartZ=0 EndX=1.7 EndY=6 EndZ=0
    g4: LineSegment StartX=1.7 StartY=6 StartZ=0 EndX=1.7 EndY=0 EndZ=0
    g5: LineSegment StartX=1.7 StartY=0 StartZ=0 EndX=0 EndY=0 EndZ=0
  constraints (17):
    c: Coincident(g-1,g0)
    c: PointOnObject(g0,g-2)
    c: Coincident(g0,g1)
    c: Horizontal(g1)
    c: Coincident(g1,g2)
    c: Vertical(g2)
    c: Coincident(g2,g3)
    c: Horizontal(g3)
    c: Coincident(g3,g4)
    c: PointOnObject(g4,g-1)
    c: Vertical(g4)
    c: Coincident(g4,g5)
    c: Coincident(g5,g0)
    c: DistanceX(g4) = 1.7
    c: DistanceY(g0) = 8
    c: DistanceX(g1,g1) = 4
    c: DistanceY(g2,g2) = 2
FEATURE [PartDesign::Revolution] Revolution003
  Angle = 360
  Angle2 = 60
  Axis = (0,0,1)
  Base = (0,0,0)
  Placement = pos=(0,0,0) rot=(0.57735,0.57735,0.57735;2.0944rad)
  Profile = -> Sketch096
  ReferenceAxis = -> Sketch096 [V_Axis]
  Reversed = true
  Suppressed = false
  Type = 0
FEATURE [PartDesign::Body] Body027
  Group = -> [Sketch096,Revolution003]
  Origin = -> Origin028
  Tip = -> Revolution003
COMPONENT P23 — recipe-attached ("Body028", modeled in this document).
Construction recipe (the document's own serialized feature program — sketch geometry with constraints, then the solid features built on it; lengths are millimeters unless a unit is written):

FEATURE [PartDesign::SubShapeBinder] Binder033
  BindCopyOnChange = 0
  BindMode = 0
  ClaimChildren = true
  Context = -> Body028 [Binder033.]
  Fuse = false
  MakeFace = true
  OffsetFill = false
  OffsetIntersection = false
  OffsetJoinType = 0
  OffsetOpenResult = false
  PartialLoad = false
  Placement = pos=(0,0,0) rot=(0.57735,0.57735,0.57735;2.0944rad)
  Relative = false
  Support = -> [Sketch097]
  _Version = 2
  expr: Placement = <<Sketch097>>.Placement
FEATURE [PartDesign::FeaturePython] BaseBend022  # WARN: FeaturePython — macro-defined, semantics opaque (R4)
  BendSide = 0
  BendSketch = -> Binder033
  MidPlane = true
  Reverse = false
  Suppressed = false
  length = 80
  radius = 2
  thickness = 0.7
FEATURE [PartDesign::Boolean] Boolean035
  BaseFeature = -> BaseBend022
  Group = -> [Compound032]
  Suppressed = false
  Type = 1
  UsePlacement = true
FEATURE [PartDesign::Boolean] Boolean036
  BaseFeature = -> Boolean035
  Group = -> [Compound033]
  Suppressed = false
  Type = 0
  UsePlacement = true
FEATURE [PartDesign::Body] Body028
  Group = -> [Binder033,BaseBend022,Boolean035,Boolean036]
  Origin = -> Origin029
  Tip = -> Boolean036
COMPONENT P24 — recipe-attached ("Body029", modeled in this document).
Construction recipe (the document's own serialized feature program — sketch geometry with constraints, then the solid features built on it; lengths are millimeters unless a unit is written):

FEATURE [PartDesign::SubShapeBinder] Binder034
  BindCopyOnChange = 0
  BindMode = 0
  ClaimChildren = true
  Context = -> Body029 [Binder034.]
  Fuse = false
  MakeFace = true
  OffsetFill = false
  OffsetIntersection = false
  OffsetJoinType = 0
  OffsetOpenResult = false
  PartialLoad = false
  Relative = false
  Support = -> [Sketch103]
  _Version = 2
FEATURE [PartDesign::FeaturePython] BaseBend023  # WARN: FeaturePython — macro-defined, semantics opaque (R4)
  BendSide = 0
  BendSketch = -> Binder034
  MidPlane = false
  Reverse = false
  Suppressed = false
  length = 100
  radius = 3
  thickness = 5
FEATURE [PartDesign::Body] Body029
  Group = -> [Binder034,BaseBend023]
  Origin = -> Origin030
  Tip = -> BaseBend023
COMPONENT P25 — recipe-attached ("Body030", modeled in this document).
Construction recipe (the document's own serialized feature program — sketch geometry with constraints, then the solid features built on it; lengths are millimeters unless a unit is written):

FEATURE [PartDesign::SubShapeBinder] Binder035
  BindCopyOnChange = 0
  BindMode = 0
  ClaimChildren = true
  Context = -> Body030 [Binder035.]
  Fuse = false
  MakeFace = true
  OffsetFill = false
  OffsetIntersection = false
  OffsetJoinType = 0
  OffsetOpenResult = false
  PartialLoad = false
  Relative = false
  Support = -> [Sketch104]
  _Version = 2
FEATURE [PartDesign::Pad] Pad024
  Direction = (0,0,1)
  Length = 5
  Length2 = 10
  Profile = -> Binder035
  Suppressed = false
  Type = 0
FEATURE [PartDesign::Body] Body030
  Group = -> [Binder035,Pad024]
  Origin = -> Origin031
  Tip = -> Pad024
COMPONENT P26 — recipe-attached ("water_sensor_spacer", modeled in this document).
Construction recipe (the document's own serialized feature program — sketch geometry with constraints, then the solid features built on it; lengths are millimeters unless a unit is written):

FEATURE [Sketcher::SketchObject] Sketch107
  AttachmentSupport = -> [XY_Plane032]
  FullyConstrained = true
  MapMode = 5
  sketch-geometry (7):
    g0: ArcOfCircle CenterX=0 CenterY=0 CenterZ=0 NormalX=0 NormalY=0 NormalZ=1 AngleXU=0 Radius=5 StartAngle=4.71239 EndAngle=6.28319
    g1: ArcOfCircle CenterX=0 CenterY=0 CenterZ=0 NormalX=0 NormalY=0 NormalZ=1 AngleXU=0 Radius=9 StartAngle=4.71239 EndAngle=6.28319
    g2: LineSegment StartX=-1.7e-15 StartY=-9 StartZ=0 EndX=-9e-16 EndY=-5 EndZ=0
    g3: LineSegment StartX=5 StartY=-1.2e-15 StartZ=0 EndX=5 EndY=9 EndZ=0
    g4: LineSegment StartX=5 StartY=9 StartZ=0 EndX=9 EndY=9 EndZ=0
    g5: LineSegment StartX=9 StartY=9 StartZ=0 EndX=9 EndY=-1.8e-15 EndZ=0
    g6: LineSegment StartX=9 StartY=-1.8e-15 StartZ=0 EndX=9 EndY=-9 EndZ=0
  constraints (20):
    c: Coincident(g0,g-1)
    c: PointOnObject(g0,g-1)
    c: PointOnObject(g0,g-2)
    c: Coincident(g1,g0)
    c: PointOnObject(g1,g-1)
    c: PointOnObject(g1,g-2)
    c: Diameter(g0) = 10
    c: Diameter(g1) = 18
    c: Coincident(g2,g1)
    c: Coincident(g2,g0)
    c: Tangent(g0,g3) = -1.5708
    c: Coincident(g3,g4)
    c: Horizontal(g4)
    c: Coincident(g4,g5)
    c: Coincident(g5,g1)
    c: Vertical(g5)
    c: Coincident(g1,g6)
    c: Vertical(g6)
    c: Horizontal(g6,g1)
    c: Equal(g6,g5)
FEATURE [PartDesign::Pad] Pad025
  Direction = (0,0,1)
  Length = 5
  Length2 = 10
  Profile = -> Sketch107
  ReferenceAxis = -> Sketch107 [N_Axis]
  Suppressed = false
  Type = 0
FEATURE [PartDesign::Mirrored] Mirrored005
  BaseFeature = -> Pad025
  MirrorPlane = -> Sketch107 [V_Axis]
  Originals = -> [Pad025]
  Suppressed = false
FEATURE [PartDesign::Body] Body031  label="water_sensor_spacer"
  Group = -> [Sketch107,Pad025,Mirrored005]
  Origin = -> Origin032
  Tip = -> Mirrored005
COMPONENT P27 — recipe-attached ("module_Body", modeled in this document).
Construction recipe (the document's own serialized feature program — sketch geometry with constraints, then the solid features built on it; lengths are millimeters unless a unit is written):

FEATURE [PartDesign::SubShapeBinder] Binder
  BindCopyOnChange = 0
  BindMode = 0
  ClaimChildren = true
  Context = -> Body [Binder.]
  Fuse = false
  MakeFace = true
  OffsetFill = false
  OffsetIntersection = false
  OffsetJoinType = 0
  OffsetOpenResult = false
  PartialLoad = false
  Relative = false
  Support = -> [Connect]
  _Version = 2
FEATURE [PartDesign::FeaturePython] BaseBend  # WARN: FeaturePython — macro-defined, semantics opaque (R4)
  BendSide = 0
  BendSketch = -> Binder
  MidPlane = false
  Reverse = false
  Suppressed = false
  length = 715
  radius = 0.1
  thickness = 0.3
FEATURE [PartDesign::FeaturePython] Extend  # WARN: FeaturePython — macro-defined, semantics opaque (R4)
  BaseFeature = -> BaseBend
  Offset = 0.02
  Refine = true
  Suppressed = false
  UseSubtraction = false
  baseObject = -> BaseBend [Face1]
  gap1 = 0
  gap2 = 0
  length = 0
FEATURE [PartDesign::FeaturePython] Bend  # WARN: FeaturePython — macro-defined, semantics opaque (R4)
  AutoMiter = false
  BaseFeature = -> Extend
  BendType = 0
  LengthList = [0.1]
  LengthSpec = 0
  ReliefFactor = 0.7
  Suppressed = false
  UseReliefFactor = false
  angle = 90
  baseObject = -> Extend [Edge4,Edge17,Edge75,Edge46,Edge63]
  bendAList = [90]
  extend1 = 0
  extend2 = 0
  gap1 = 0
  gap2 = 0
  invert = true
  kfactor = 0.5
  length = 0.1
  maxExtendDist = 2.5
  minGap = 0.1
  minReliefGap = 1.5
  miterangle1 = 0
  miterangle2 = 0
  offset = 0
  radius = 0.1
  reliefType = 0
  reliefd = 1
  reliefw = 0.8
  sketchflip = false
  sketchinvert = false
  unfold = false
  expr: radius = BaseBend.radius
FEATURE [PartDesign::Boolean] Boolean007
  BaseFeature = -> Bend
  Group = -> [Compound010]
  Refine = true
  Suppressed = false
  Type = 0
  UsePlacement = true
FEATURE [PartDesign::Boolean] Boolean
  BaseFeature = -> Boolean007
  Group = -> [Compound001]
  Suppressed = false
  Type = 1
  UsePlacement = true
FEATURE [PartDesign::CoordinateSystem] Local_CS005  label="face_sink_LCS"
  AttacherType = Attacher::AttachEngine3D
  AttachmentOffset = pos=(0,70,121) rot=(0,0,1;0rad)
  AttachmentSupport = -> [XY_Plane]
  MapMode = 5
  Placement = pos=(0,70,121) rot=(0,0,1;0rad)
  expr: AttachmentOffset = <<sink_placement>>.Placement
FEATURE [PartDesign::CoordinateSystem] Local_CS006  label="face_lamp_holder_LCS"
  AttacherType = Attacher::AttachEngine3D
  AttachmentOffset = pos=(0,70,172) rot=(0,0,1;0rad)
  AttachmentSupport = -> [XY_Plane]
  MapMode = 5
  Placement = pos=(0,70,172) rot=(0,0,1;0rad)
  expr: AttachmentOffset = <<lamp_holder_placement>>.Placement
FEATURE [PartDesign::CoordinateSystem] Local_CS007  label="face_back_LCS"
  AttacherType = Attacher::AttachEngine3D
  AttachmentSupport = -> [XY_Plane]
  MapMode = 5
FEATURE [PartDesign::CoordinateSystem] Local_CS008  label="face_top_LCS"
  AttacherType = Attacher::AttachEngine3D
  AttachmentOffset = pos=(0,70,715.1) rot=(0,0,1;0rad)
  AttachmentSupport = -> [XY_Plane]
  MapMode = 5
  Placement = pos=(0,70,715.1) rot=(0,0,1;0rad)
  expr: AttachmentOffset = <<top_placement>>.Placement
FEATURE [PartDesign::CoordinateSystem] Local_CS009  label="face_cap_LCS"
  AttacherType = Attacher::AttachEngine3D
  AttachmentOffset = pos=(0,0,715) rot=(0,0,1;0rad)
  AttachmentSupport = -> [XY_Plane]
  MapMode = 5
  Placement = pos=(0,0,715) rot=(0,0,1;0rad)
  expr: AttachmentOffset = <<cap_placement>>.Placement
FEATURE [PartDesign::CoordinateSystem] Local_CS020  label="face_LCS"
  AttacherType = Attacher::AttachEngine3D
  AttachmentSupport = -> [XY_Plane]
  MapMode = 5
FEATURE [PartDesign::CoordinateSystem] Local_CS027
  AttacherType = Attacher::AttachEngine3D
  AttachmentOffset = pos=(299.78,198,16) rot=(0,0,1;0rad)
  AttachmentSupport = -> [XY_Plane]
  MapMode = 5
  Placement = pos=(299.78,198,16) rot=(0,0,1;0rad)
  expr: AttachmentOffset = <<face_magnet_fix_placement>>.Placement
FEATURE [PartDesign::Boolean] Boolean033
  BaseFeature = -> Boolean
  Group = -> [Compound029]
  Refine = true
  Suppressed = false
  Type = 0
  UsePlacement = true
FEATURE [PartDesign::Body] Body  label="face"
  Group = -> [Binder,BaseBend,Extend,Bend,Boolean007,Local_CS005,Local_CS006,Local_CS007,Local_CS008,Local_CS009,Local_CS020,Local_CS027,Boolean,Boolean033]
  Origin = -> Origin
  Tip = -> Boolean033
COMPONENT P28 — geometry summary ("modules"; no construction recipe available for this part):
  bounding box: 581.5 x 570.0 x 137.2 mm
  tessellated surface: 359,856 triangles
  volume: 1120940 mm^3 (2% of its bounding box)
  symmetry: mirror-symmetric across its x mid-plane
PROVENANCE & LICENSES
A FreeCAD (.FCStd) document from a public repository crawl; recipes are the document's own serialized feature recipes (and, for linked parts, companion documents' recipes).
License: as declared in the source repository (recorded in the dataset sidecar).
